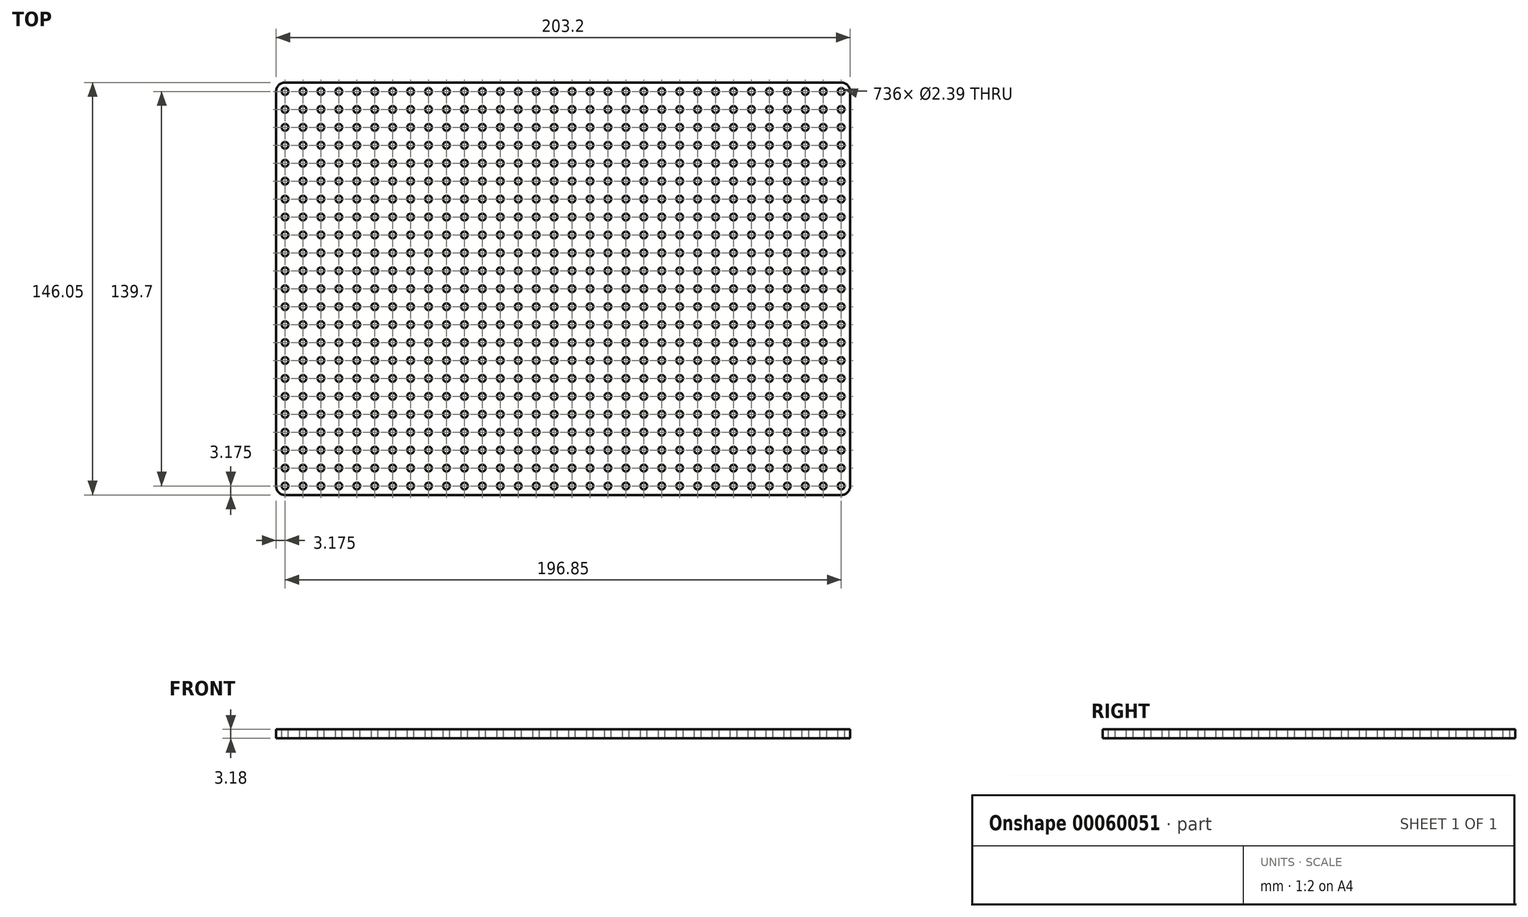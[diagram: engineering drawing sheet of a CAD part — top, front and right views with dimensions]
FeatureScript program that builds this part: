
annotation { "Feature Type Name" : "Feature", "Feature Type Description" : "" }
export const myFeature = defineFeature(function(context is Context, id is Id, definition is map)
    precondition{}
    {
        {
            var Q0;
            Q0=qCreatedBy(makeId("Top.planeOp"),FACE);
            var sketch = newSketch(context, id + "F0", { "sketchPlane" : qUnion([Q0])});
            skLineSegment(sketch, "E0.bottom", {"start": v(3.17, 0) * mm, "end": v(200.03, 0) * mm});
            skLineSegment(sketch, "E0.top", {"start": v(3.17, 146.05) * mm, "end": v(200.03, 146.05) * mm});
            skLineSegment(sketch, "E0.left", {"start": v(0, 3.17) * mm, "end": v(0, 142.87) * mm});
            skLineSegment(sketch, "E0.right", {"start": v(203.2, 3.17) * mm, "end": v(203.2, 142.87) * mm});
            skPoint(sketch, "E1.visualSharp", {"position": v(0, 146.05) * mm});
            skArc(sketch, "E1.filletArc", {"start": v(3.17, 146.05) * mm, "mid": v(0.93, 145.12) * mm, "end": v(0, 142.87) * mm});
            skPoint(sketch, "E2.visualSharp", {"position": v(203.2, 146.05) * mm});
            skArc(sketch, "E2.filletArc", {"start": v(203.2, 142.87) * mm, "mid": v(202.27, 145.12) * mm, "end": v(200.03, 146.05) * mm});
            skPoint(sketch, "E3.visualSharp", {"position": v(203.2, 0) * mm});
            skArc(sketch, "E3.filletArc", {"start": v(200.03, 0) * mm, "mid": v(202.27, 0.93) * mm, "end": v(203.2, 3.17) * mm});
            skPoint(sketch, "E4.visualSharp", {"position": v(0, 0) * mm});
            skArc(sketch, "E4.filletArc", {"start": v(0, 3.17) * mm, "mid": v(0.93, 0.93) * mm, "end": v(3.17, 0) * mm});
            skSolve(sketch);
        }
        {
            var Q0;
            Q0=makeQuery(id+"F0.imprint","IMPRINT",FACE,{"disambiguationData":[TD([[makeQuery(id+"F0.imprint","IMPRINT",EDGE,{"derivedFrom":sQuery(id+"F0.wireOp",EDGE,"E0.bottom")}),1.0]])]});
            extrude(context, id + "F1", {"entities" : qUnion([Q0]), "depth" : 3.17 * mm});
        }
        {
            var Q0;
            Q0=makeQuery(id+"F1.opExtrude","CAP_FACE",FACE,{"disambiguationData":[OSD([sQuery(id+"F0.wireOp",EDGE,"E0.bottom"),sQuery(id+"F0.wireOp",EDGE,"E0.top"),sQuery(id+"F0.wireOp",EDGE,"E0.left"),sQuery(id+"F0.wireOp",EDGE,"E0.right"),sQuery(id+"F0.wireOp",EDGE,"E1.filletArc"),sQuery(id+"F0.wireOp",EDGE,"E2.filletArc"),sQuery(id+"F0.wireOp",EDGE,"E3.filletArc"),sQuery(id+"F0.wireOp",EDGE,"E4.filletArc")])],"isStart":false});
            var sketch = newSketch(context, id + "F2", { "sketchPlane" : qUnion([Q0])});
            skCircle(sketch, "E5", {"center": v(3.17, 3.17) * mm, "radius": 1.2 * mm});
            skCircle(sketch, "E6.0.1.0", {"center": v(3.17, 9.53) * mm, "radius": 1.2 * mm});
            skCircle(sketch, "E6.0.2.0", {"center": v(3.17, 15.88) * mm, "radius": 1.2 * mm});
            skCircle(sketch, "E6.0.3.0", {"center": v(3.17, 22.23) * mm, "radius": 1.2 * mm});
            skCircle(sketch, "E6.0.4.0", {"center": v(3.17, 28.58) * mm, "radius": 1.2 * mm});
            skCircle(sketch, "E6.0.5.0", {"center": v(3.17, 34.92) * mm, "radius": 1.2 * mm});
            skCircle(sketch, "E6.0.6.0", {"center": v(3.17, 41.27) * mm, "radius": 1.2 * mm});
            skCircle(sketch, "E6.0.7.0", {"center": v(3.17, 47.62) * mm, "radius": 1.2 * mm});
            skCircle(sketch, "E6.0.8.0", {"center": v(3.17, 53.98) * mm, "radius": 1.2 * mm});
            skCircle(sketch, "E6.0.9.0", {"center": v(3.17, 60.33) * mm, "radius": 1.2 * mm});
            skCircle(sketch, "E6.0.10.0", {"center": v(3.17, 66.67) * mm, "radius": 1.2 * mm});
            skCircle(sketch, "E6.0.11.0", {"center": v(3.17, 73.03) * mm, "radius": 1.2 * mm});
            skCircle(sketch, "E6.0.12.0", {"center": v(3.17, 79.38) * mm, "radius": 1.2 * mm});
            skCircle(sketch, "E6.0.13.0", {"center": v(3.17, 85.73) * mm, "radius": 1.2 * mm});
            skCircle(sketch, "E6.0.14.0", {"center": v(3.17, 92.08) * mm, "radius": 1.2 * mm});
            skCircle(sketch, "E6.0.15.0", {"center": v(3.17, 98.43) * mm, "radius": 1.2 * mm});
            skCircle(sketch, "E6.0.16.0", {"center": v(3.17, 104.78) * mm, "radius": 1.2 * mm});
            skCircle(sketch, "E6.0.17.0", {"center": v(3.17, 111.12) * mm, "radius": 1.2 * mm});
            skCircle(sketch, "E6.0.18.0", {"center": v(3.17, 117.48) * mm, "radius": 1.2 * mm});
            skCircle(sketch, "E6.0.19.0", {"center": v(3.17, 123.83) * mm, "radius": 1.2 * mm});
            skCircle(sketch, "E6.0.20.0", {"center": v(3.17, 130.18) * mm, "radius": 1.2 * mm});
            skCircle(sketch, "E6.0.21.0", {"center": v(3.17, 136.53) * mm, "radius": 1.2 * mm});
            skCircle(sketch, "E6.0.22.0", {"center": v(3.17, 142.88) * mm, "radius": 1.2 * mm});
            skCircle(sketch, "E6.1.0.0", {"center": v(9.53, 3.17) * mm, "radius": 1.2 * mm});
            skCircle(sketch, "E6.1.1.0", {"center": v(9.53, 9.53) * mm, "radius": 1.2 * mm});
            skCircle(sketch, "E6.1.2.0", {"center": v(9.53, 15.88) * mm, "radius": 1.2 * mm});
            skCircle(sketch, "E6.1.3.0", {"center": v(9.53, 22.23) * mm, "radius": 1.2 * mm});
            skCircle(sketch, "E6.1.4.0", {"center": v(9.53, 28.58) * mm, "radius": 1.2 * mm});
            skCircle(sketch, "E6.1.5.0", {"center": v(9.53, 34.92) * mm, "radius": 1.2 * mm});
            skCircle(sketch, "E6.1.6.0", {"center": v(9.53, 41.27) * mm, "radius": 1.2 * mm});
            skCircle(sketch, "E6.1.7.0", {"center": v(9.53, 47.62) * mm, "radius": 1.2 * mm});
            skCircle(sketch, "E6.1.8.0", {"center": v(9.53, 53.98) * mm, "radius": 1.2 * mm});
            skCircle(sketch, "E6.1.9.0", {"center": v(9.53, 60.33) * mm, "radius": 1.2 * mm});
            skCircle(sketch, "E6.1.10.0", {"center": v(9.53, 66.67) * mm, "radius": 1.2 * mm});
            skCircle(sketch, "E6.1.11.0", {"center": v(9.53, 73.03) * mm, "radius": 1.2 * mm});
            skCircle(sketch, "E6.1.12.0", {"center": v(9.53, 79.38) * mm, "radius": 1.2 * mm});
            skCircle(sketch, "E6.1.13.0", {"center": v(9.53, 85.73) * mm, "radius": 1.2 * mm});
            skCircle(sketch, "E6.1.14.0", {"center": v(9.53, 92.08) * mm, "radius": 1.2 * mm});
            skCircle(sketch, "E6.1.15.0", {"center": v(9.53, 98.43) * mm, "radius": 1.2 * mm});
            skCircle(sketch, "E6.1.16.0", {"center": v(9.53, 104.78) * mm, "radius": 1.2 * mm});
            skCircle(sketch, "E6.1.17.0", {"center": v(9.53, 111.12) * mm, "radius": 1.2 * mm});
            skCircle(sketch, "E6.1.18.0", {"center": v(9.53, 117.48) * mm, "radius": 1.2 * mm});
            skCircle(sketch, "E6.1.19.0", {"center": v(9.53, 123.83) * mm, "radius": 1.2 * mm});
            skCircle(sketch, "E6.1.20.0", {"center": v(9.53, 130.18) * mm, "radius": 1.2 * mm});
            skCircle(sketch, "E6.1.21.0", {"center": v(9.53, 136.53) * mm, "radius": 1.2 * mm});
            skCircle(sketch, "E6.1.22.0", {"center": v(9.53, 142.88) * mm, "radius": 1.2 * mm});
            skCircle(sketch, "E6.2.0.0", {"center": v(15.88, 3.17) * mm, "radius": 1.2 * mm});
            skCircle(sketch, "E6.2.1.0", {"center": v(15.88, 9.53) * mm, "radius": 1.2 * mm});
            skCircle(sketch, "E6.2.2.0", {"center": v(15.88, 15.88) * mm, "radius": 1.2 * mm});
            skCircle(sketch, "E6.2.3.0", {"center": v(15.88, 22.23) * mm, "radius": 1.2 * mm});
            skCircle(sketch, "E6.2.4.0", {"center": v(15.88, 28.58) * mm, "radius": 1.2 * mm});
            skCircle(sketch, "E6.2.5.0", {"center": v(15.88, 34.92) * mm, "radius": 1.2 * mm});
            skCircle(sketch, "E6.2.6.0", {"center": v(15.88, 41.27) * mm, "radius": 1.2 * mm});
            skCircle(sketch, "E6.2.7.0", {"center": v(15.88, 47.62) * mm, "radius": 1.2 * mm});
            skCircle(sketch, "E6.2.8.0", {"center": v(15.88, 53.98) * mm, "radius": 1.2 * mm});
            skCircle(sketch, "E6.2.9.0", {"center": v(15.88, 60.33) * mm, "radius": 1.2 * mm});
            skCircle(sketch, "E6.2.10.0", {"center": v(15.88, 66.67) * mm, "radius": 1.2 * mm});
            skCircle(sketch, "E6.2.11.0", {"center": v(15.88, 73.03) * mm, "radius": 1.2 * mm});
            skCircle(sketch, "E6.2.12.0", {"center": v(15.88, 79.38) * mm, "radius": 1.2 * mm});
            skCircle(sketch, "E6.2.13.0", {"center": v(15.88, 85.73) * mm, "radius": 1.2 * mm});
            skCircle(sketch, "E6.2.14.0", {"center": v(15.88, 92.08) * mm, "radius": 1.2 * mm});
            skCircle(sketch, "E6.2.15.0", {"center": v(15.88, 98.43) * mm, "radius": 1.2 * mm});
            skCircle(sketch, "E6.2.16.0", {"center": v(15.88, 104.78) * mm, "radius": 1.2 * mm});
            skCircle(sketch, "E6.2.17.0", {"center": v(15.88, 111.12) * mm, "radius": 1.2 * mm});
            skCircle(sketch, "E6.2.18.0", {"center": v(15.88, 117.48) * mm, "radius": 1.2 * mm});
            skCircle(sketch, "E6.2.19.0", {"center": v(15.88, 123.83) * mm, "radius": 1.2 * mm});
            skCircle(sketch, "E6.2.20.0", {"center": v(15.88, 130.18) * mm, "radius": 1.2 * mm});
            skCircle(sketch, "E6.2.21.0", {"center": v(15.88, 136.53) * mm, "radius": 1.2 * mm});
            skCircle(sketch, "E6.2.22.0", {"center": v(15.88, 142.88) * mm, "radius": 1.2 * mm});
            skCircle(sketch, "E6.3.0.0", {"center": v(22.23, 3.17) * mm, "radius": 1.2 * mm});
            skCircle(sketch, "E6.3.1.0", {"center": v(22.23, 9.53) * mm, "radius": 1.2 * mm});
            skCircle(sketch, "E6.3.2.0", {"center": v(22.23, 15.88) * mm, "radius": 1.2 * mm});
            skCircle(sketch, "E6.3.3.0", {"center": v(22.23, 22.23) * mm, "radius": 1.2 * mm});
            skCircle(sketch, "E6.3.4.0", {"center": v(22.23, 28.58) * mm, "radius": 1.2 * mm});
            skCircle(sketch, "E6.3.5.0", {"center": v(22.23, 34.92) * mm, "radius": 1.2 * mm});
            skCircle(sketch, "E6.3.6.0", {"center": v(22.23, 41.27) * mm, "radius": 1.2 * mm});
            skCircle(sketch, "E6.3.7.0", {"center": v(22.23, 47.62) * mm, "radius": 1.2 * mm});
            skCircle(sketch, "E6.3.8.0", {"center": v(22.23, 53.98) * mm, "radius": 1.2 * mm});
            skCircle(sketch, "E6.3.9.0", {"center": v(22.23, 60.33) * mm, "radius": 1.2 * mm});
            skCircle(sketch, "E6.3.10.0", {"center": v(22.23, 66.67) * mm, "radius": 1.2 * mm});
            skCircle(sketch, "E6.3.11.0", {"center": v(22.23, 73.03) * mm, "radius": 1.2 * mm});
            skCircle(sketch, "E6.3.12.0", {"center": v(22.23, 79.38) * mm, "radius": 1.2 * mm});
            skCircle(sketch, "E6.3.13.0", {"center": v(22.23, 85.73) * mm, "radius": 1.2 * mm});
            skCircle(sketch, "E6.3.14.0", {"center": v(22.23, 92.08) * mm, "radius": 1.2 * mm});
            skCircle(sketch, "E6.3.15.0", {"center": v(22.23, 98.43) * mm, "radius": 1.2 * mm});
            skCircle(sketch, "E6.3.16.0", {"center": v(22.23, 104.78) * mm, "radius": 1.2 * mm});
            skCircle(sketch, "E6.3.17.0", {"center": v(22.23, 111.12) * mm, "radius": 1.2 * mm});
            skCircle(sketch, "E6.3.18.0", {"center": v(22.23, 117.48) * mm, "radius": 1.2 * mm});
            skCircle(sketch, "E6.3.19.0", {"center": v(22.23, 123.83) * mm, "radius": 1.2 * mm});
            skCircle(sketch, "E6.3.20.0", {"center": v(22.23, 130.18) * mm, "radius": 1.2 * mm});
            skCircle(sketch, "E6.3.21.0", {"center": v(22.23, 136.53) * mm, "radius": 1.2 * mm});
            skCircle(sketch, "E6.3.22.0", {"center": v(22.23, 142.88) * mm, "radius": 1.2 * mm});
            skCircle(sketch, "E6.4.0.0", {"center": v(28.58, 3.17) * mm, "radius": 1.2 * mm});
            skCircle(sketch, "E6.4.1.0", {"center": v(28.58, 9.53) * mm, "radius": 1.2 * mm});
            skCircle(sketch, "E6.4.2.0", {"center": v(28.58, 15.88) * mm, "radius": 1.2 * mm});
            skCircle(sketch, "E6.4.3.0", {"center": v(28.58, 22.23) * mm, "radius": 1.2 * mm});
            skCircle(sketch, "E6.4.4.0", {"center": v(28.58, 28.58) * mm, "radius": 1.2 * mm});
            skCircle(sketch, "E6.4.5.0", {"center": v(28.58, 34.92) * mm, "radius": 1.2 * mm});
            skCircle(sketch, "E6.4.6.0", {"center": v(28.58, 41.27) * mm, "radius": 1.2 * mm});
            skCircle(sketch, "E6.4.7.0", {"center": v(28.58, 47.62) * mm, "radius": 1.2 * mm});
            skCircle(sketch, "E6.4.8.0", {"center": v(28.58, 53.98) * mm, "radius": 1.2 * mm});
            skCircle(sketch, "E6.4.9.0", {"center": v(28.58, 60.33) * mm, "radius": 1.2 * mm});
            skCircle(sketch, "E6.4.10.0", {"center": v(28.58, 66.67) * mm, "radius": 1.2 * mm});
            skCircle(sketch, "E6.4.11.0", {"center": v(28.58, 73.03) * mm, "radius": 1.2 * mm});
            skCircle(sketch, "E6.4.12.0", {"center": v(28.58, 79.38) * mm, "radius": 1.2 * mm});
            skCircle(sketch, "E6.4.13.0", {"center": v(28.58, 85.73) * mm, "radius": 1.2 * mm});
            skCircle(sketch, "E6.4.14.0", {"center": v(28.58, 92.08) * mm, "radius": 1.2 * mm});
            skCircle(sketch, "E6.4.15.0", {"center": v(28.58, 98.43) * mm, "radius": 1.2 * mm});
            skCircle(sketch, "E6.4.16.0", {"center": v(28.58, 104.78) * mm, "radius": 1.2 * mm});
            skCircle(sketch, "E6.4.17.0", {"center": v(28.58, 111.12) * mm, "radius": 1.2 * mm});
            skCircle(sketch, "E6.4.18.0", {"center": v(28.58, 117.48) * mm, "radius": 1.2 * mm});
            skCircle(sketch, "E6.4.19.0", {"center": v(28.58, 123.83) * mm, "radius": 1.2 * mm});
            skCircle(sketch, "E6.4.20.0", {"center": v(28.58, 130.18) * mm, "radius": 1.2 * mm});
            skCircle(sketch, "E6.4.21.0", {"center": v(28.58, 136.53) * mm, "radius": 1.2 * mm});
            skCircle(sketch, "E6.4.22.0", {"center": v(28.58, 142.88) * mm, "radius": 1.2 * mm});
            skCircle(sketch, "E6.5.0.0", {"center": v(34.92, 3.17) * mm, "radius": 1.2 * mm});
            skCircle(sketch, "E6.5.1.0", {"center": v(34.92, 9.53) * mm, "radius": 1.2 * mm});
            skCircle(sketch, "E6.5.2.0", {"center": v(34.92, 15.88) * mm, "radius": 1.2 * mm});
            skCircle(sketch, "E6.5.3.0", {"center": v(34.92, 22.23) * mm, "radius": 1.2 * mm});
            skCircle(sketch, "E6.5.4.0", {"center": v(34.92, 28.58) * mm, "radius": 1.2 * mm});
            skCircle(sketch, "E6.5.5.0", {"center": v(34.92, 34.92) * mm, "radius": 1.2 * mm});
            skCircle(sketch, "E6.5.6.0", {"center": v(34.92, 41.27) * mm, "radius": 1.2 * mm});
            skCircle(sketch, "E6.5.7.0", {"center": v(34.92, 47.62) * mm, "radius": 1.2 * mm});
            skCircle(sketch, "E6.5.8.0", {"center": v(34.92, 53.98) * mm, "radius": 1.2 * mm});
            skCircle(sketch, "E6.5.9.0", {"center": v(34.92, 60.33) * mm, "radius": 1.2 * mm});
            skCircle(sketch, "E6.5.10.0", {"center": v(34.92, 66.67) * mm, "radius": 1.2 * mm});
            skCircle(sketch, "E6.5.11.0", {"center": v(34.92, 73.03) * mm, "radius": 1.2 * mm});
            skCircle(sketch, "E6.5.12.0", {"center": v(34.92, 79.38) * mm, "radius": 1.2 * mm});
            skCircle(sketch, "E6.5.13.0", {"center": v(34.92, 85.73) * mm, "radius": 1.2 * mm});
            skCircle(sketch, "E6.5.14.0", {"center": v(34.92, 92.08) * mm, "radius": 1.2 * mm});
            skCircle(sketch, "E6.5.15.0", {"center": v(34.92, 98.43) * mm, "radius": 1.2 * mm});
            skCircle(sketch, "E6.5.16.0", {"center": v(34.92, 104.78) * mm, "radius": 1.2 * mm});
            skCircle(sketch, "E6.5.17.0", {"center": v(34.92, 111.12) * mm, "radius": 1.2 * mm});
            skCircle(sketch, "E6.5.18.0", {"center": v(34.92, 117.48) * mm, "radius": 1.2 * mm});
            skCircle(sketch, "E6.5.19.0", {"center": v(34.92, 123.83) * mm, "radius": 1.2 * mm});
            skCircle(sketch, "E6.5.20.0", {"center": v(34.92, 130.18) * mm, "radius": 1.2 * mm});
            skCircle(sketch, "E6.5.21.0", {"center": v(34.92, 136.53) * mm, "radius": 1.2 * mm});
            skCircle(sketch, "E6.5.22.0", {"center": v(34.92, 142.88) * mm, "radius": 1.2 * mm});
            skCircle(sketch, "E6.6.0.0", {"center": v(41.27, 3.17) * mm, "radius": 1.2 * mm});
            skCircle(sketch, "E6.6.1.0", {"center": v(41.27, 9.53) * mm, "radius": 1.2 * mm});
            skCircle(sketch, "E6.6.2.0", {"center": v(41.27, 15.88) * mm, "radius": 1.2 * mm});
            skCircle(sketch, "E6.6.3.0", {"center": v(41.27, 22.23) * mm, "radius": 1.2 * mm});
            skCircle(sketch, "E6.6.4.0", {"center": v(41.27, 28.58) * mm, "radius": 1.2 * mm});
            skCircle(sketch, "E6.6.5.0", {"center": v(41.27, 34.92) * mm, "radius": 1.2 * mm});
            skCircle(sketch, "E6.6.6.0", {"center": v(41.27, 41.27) * mm, "radius": 1.2 * mm});
            skCircle(sketch, "E6.6.7.0", {"center": v(41.27, 47.62) * mm, "radius": 1.2 * mm});
            skCircle(sketch, "E6.6.8.0", {"center": v(41.27, 53.98) * mm, "radius": 1.2 * mm});
            skCircle(sketch, "E6.6.9.0", {"center": v(41.27, 60.33) * mm, "radius": 1.2 * mm});
            skCircle(sketch, "E6.6.10.0", {"center": v(41.27, 66.67) * mm, "radius": 1.2 * mm});
            skCircle(sketch, "E6.6.11.0", {"center": v(41.27, 73.03) * mm, "radius": 1.2 * mm});
            skCircle(sketch, "E6.6.12.0", {"center": v(41.27, 79.38) * mm, "radius": 1.2 * mm});
            skCircle(sketch, "E6.6.13.0", {"center": v(41.27, 85.73) * mm, "radius": 1.2 * mm});
            skCircle(sketch, "E6.6.14.0", {"center": v(41.27, 92.08) * mm, "radius": 1.2 * mm});
            skCircle(sketch, "E6.6.15.0", {"center": v(41.27, 98.43) * mm, "radius": 1.2 * mm});
            skCircle(sketch, "E6.6.16.0", {"center": v(41.27, 104.78) * mm, "radius": 1.2 * mm});
            skCircle(sketch, "E6.6.17.0", {"center": v(41.27, 111.12) * mm, "radius": 1.2 * mm});
            skCircle(sketch, "E6.6.18.0", {"center": v(41.27, 117.48) * mm, "radius": 1.2 * mm});
            skCircle(sketch, "E6.6.19.0", {"center": v(41.27, 123.83) * mm, "radius": 1.2 * mm});
            skCircle(sketch, "E6.6.20.0", {"center": v(41.27, 130.18) * mm, "radius": 1.2 * mm});
            skCircle(sketch, "E6.6.21.0", {"center": v(41.27, 136.53) * mm, "radius": 1.2 * mm});
            skCircle(sketch, "E6.6.22.0", {"center": v(41.27, 142.88) * mm, "radius": 1.2 * mm});
            skCircle(sketch, "E6.7.0.0", {"center": v(47.62, 3.17) * mm, "radius": 1.2 * mm});
            skCircle(sketch, "E6.7.1.0", {"center": v(47.62, 9.53) * mm, "radius": 1.2 * mm});
            skCircle(sketch, "E6.7.2.0", {"center": v(47.62, 15.88) * mm, "radius": 1.2 * mm});
            skCircle(sketch, "E6.7.3.0", {"center": v(47.62, 22.23) * mm, "radius": 1.2 * mm});
            skCircle(sketch, "E6.7.4.0", {"center": v(47.62, 28.58) * mm, "radius": 1.2 * mm});
            skCircle(sketch, "E6.7.5.0", {"center": v(47.62, 34.92) * mm, "radius": 1.2 * mm});
            skCircle(sketch, "E6.7.6.0", {"center": v(47.62, 41.27) * mm, "radius": 1.2 * mm});
            skCircle(sketch, "E6.7.7.0", {"center": v(47.62, 47.62) * mm, "radius": 1.2 * mm});
            skCircle(sketch, "E6.7.8.0", {"center": v(47.62, 53.98) * mm, "radius": 1.2 * mm});
            skCircle(sketch, "E6.7.9.0", {"center": v(47.62, 60.33) * mm, "radius": 1.2 * mm});
            skCircle(sketch, "E6.7.10.0", {"center": v(47.62, 66.67) * mm, "radius": 1.2 * mm});
            skCircle(sketch, "E6.7.11.0", {"center": v(47.62, 73.03) * mm, "radius": 1.2 * mm});
            skCircle(sketch, "E6.7.12.0", {"center": v(47.62, 79.38) * mm, "radius": 1.2 * mm});
            skCircle(sketch, "E6.7.13.0", {"center": v(47.62, 85.73) * mm, "radius": 1.2 * mm});
            skCircle(sketch, "E6.7.14.0", {"center": v(47.62, 92.08) * mm, "radius": 1.2 * mm});
            skCircle(sketch, "E6.7.15.0", {"center": v(47.62, 98.43) * mm, "radius": 1.2 * mm});
            skCircle(sketch, "E6.7.16.0", {"center": v(47.62, 104.78) * mm, "radius": 1.2 * mm});
            skCircle(sketch, "E6.7.17.0", {"center": v(47.62, 111.12) * mm, "radius": 1.2 * mm});
            skCircle(sketch, "E6.7.18.0", {"center": v(47.62, 117.48) * mm, "radius": 1.2 * mm});
            skCircle(sketch, "E6.7.19.0", {"center": v(47.62, 123.83) * mm, "radius": 1.2 * mm});
            skCircle(sketch, "E6.7.20.0", {"center": v(47.62, 130.18) * mm, "radius": 1.2 * mm});
            skCircle(sketch, "E6.7.21.0", {"center": v(47.62, 136.53) * mm, "radius": 1.2 * mm});
            skCircle(sketch, "E6.7.22.0", {"center": v(47.62, 142.88) * mm, "radius": 1.2 * mm});
            skCircle(sketch, "E6.8.0.0", {"center": v(53.98, 3.17) * mm, "radius": 1.2 * mm});
            skCircle(sketch, "E6.8.1.0", {"center": v(53.98, 9.53) * mm, "radius": 1.2 * mm});
            skCircle(sketch, "E6.8.2.0", {"center": v(53.98, 15.88) * mm, "radius": 1.2 * mm});
            skCircle(sketch, "E6.8.3.0", {"center": v(53.98, 22.23) * mm, "radius": 1.2 * mm});
            skCircle(sketch, "E6.8.4.0", {"center": v(53.98, 28.58) * mm, "radius": 1.2 * mm});
            skCircle(sketch, "E6.8.5.0", {"center": v(53.98, 34.92) * mm, "radius": 1.2 * mm});
            skCircle(sketch, "E6.8.6.0", {"center": v(53.98, 41.27) * mm, "radius": 1.2 * mm});
            skCircle(sketch, "E6.8.7.0", {"center": v(53.98, 47.62) * mm, "radius": 1.2 * mm});
            skCircle(sketch, "E6.8.8.0", {"center": v(53.98, 53.98) * mm, "radius": 1.2 * mm});
            skCircle(sketch, "E6.8.9.0", {"center": v(53.98, 60.33) * mm, "radius": 1.2 * mm});
            skCircle(sketch, "E6.8.10.0", {"center": v(53.98, 66.67) * mm, "radius": 1.2 * mm});
            skCircle(sketch, "E6.8.11.0", {"center": v(53.98, 73.03) * mm, "radius": 1.2 * mm});
            skCircle(sketch, "E6.8.12.0", {"center": v(53.98, 79.38) * mm, "radius": 1.2 * mm});
            skCircle(sketch, "E6.8.13.0", {"center": v(53.98, 85.73) * mm, "radius": 1.2 * mm});
            skCircle(sketch, "E6.8.14.0", {"center": v(53.98, 92.08) * mm, "radius": 1.2 * mm});
            skCircle(sketch, "E6.8.15.0", {"center": v(53.98, 98.43) * mm, "radius": 1.2 * mm});
            skCircle(sketch, "E6.8.16.0", {"center": v(53.98, 104.78) * mm, "radius": 1.2 * mm});
            skCircle(sketch, "E6.8.17.0", {"center": v(53.98, 111.12) * mm, "radius": 1.2 * mm});
            skCircle(sketch, "E6.8.18.0", {"center": v(53.98, 117.48) * mm, "radius": 1.2 * mm});
            skCircle(sketch, "E6.8.19.0", {"center": v(53.98, 123.83) * mm, "radius": 1.2 * mm});
            skCircle(sketch, "E6.8.20.0", {"center": v(53.98, 130.18) * mm, "radius": 1.2 * mm});
            skCircle(sketch, "E6.8.21.0", {"center": v(53.98, 136.53) * mm, "radius": 1.2 * mm});
            skCircle(sketch, "E6.8.22.0", {"center": v(53.98, 142.88) * mm, "radius": 1.2 * mm});
            skCircle(sketch, "E6.9.0.0", {"center": v(60.33, 3.17) * mm, "radius": 1.2 * mm});
            skCircle(sketch, "E6.9.1.0", {"center": v(60.33, 9.53) * mm, "radius": 1.2 * mm});
            skCircle(sketch, "E6.9.2.0", {"center": v(60.33, 15.88) * mm, "radius": 1.2 * mm});
            skCircle(sketch, "E6.9.3.0", {"center": v(60.33, 22.23) * mm, "radius": 1.2 * mm});
            skCircle(sketch, "E6.9.4.0", {"center": v(60.33, 28.58) * mm, "radius": 1.2 * mm});
            skCircle(sketch, "E6.9.5.0", {"center": v(60.33, 34.92) * mm, "radius": 1.2 * mm});
            skCircle(sketch, "E6.9.6.0", {"center": v(60.33, 41.27) * mm, "radius": 1.2 * mm});
            skCircle(sketch, "E6.9.7.0", {"center": v(60.33, 47.62) * mm, "radius": 1.2 * mm});
            skCircle(sketch, "E6.9.8.0", {"center": v(60.33, 53.98) * mm, "radius": 1.2 * mm});
            skCircle(sketch, "E6.9.9.0", {"center": v(60.33, 60.33) * mm, "radius": 1.2 * mm});
            skCircle(sketch, "E6.9.10.0", {"center": v(60.33, 66.67) * mm, "radius": 1.2 * mm});
            skCircle(sketch, "E6.9.11.0", {"center": v(60.33, 73.03) * mm, "radius": 1.2 * mm});
            skCircle(sketch, "E6.9.12.0", {"center": v(60.33, 79.38) * mm, "radius": 1.2 * mm});
            skCircle(sketch, "E6.9.13.0", {"center": v(60.33, 85.73) * mm, "radius": 1.2 * mm});
            skCircle(sketch, "E6.9.14.0", {"center": v(60.33, 92.08) * mm, "radius": 1.2 * mm});
            skCircle(sketch, "E6.9.15.0", {"center": v(60.33, 98.43) * mm, "radius": 1.2 * mm});
            skCircle(sketch, "E6.9.16.0", {"center": v(60.33, 104.78) * mm, "radius": 1.2 * mm});
            skCircle(sketch, "E6.9.17.0", {"center": v(60.33, 111.12) * mm, "radius": 1.2 * mm});
            skCircle(sketch, "E6.9.18.0", {"center": v(60.33, 117.48) * mm, "radius": 1.2 * mm});
            skCircle(sketch, "E6.9.19.0", {"center": v(60.33, 123.83) * mm, "radius": 1.2 * mm});
            skCircle(sketch, "E6.9.20.0", {"center": v(60.33, 130.18) * mm, "radius": 1.2 * mm});
            skCircle(sketch, "E6.9.21.0", {"center": v(60.33, 136.53) * mm, "radius": 1.2 * mm});
            skCircle(sketch, "E6.9.22.0", {"center": v(60.33, 142.88) * mm, "radius": 1.2 * mm});
            skCircle(sketch, "E6.10.0.0", {"center": v(66.67, 3.17) * mm, "radius": 1.2 * mm});
            skCircle(sketch, "E6.10.1.0", {"center": v(66.67, 9.53) * mm, "radius": 1.2 * mm});
            skCircle(sketch, "E6.10.2.0", {"center": v(66.67, 15.88) * mm, "radius": 1.2 * mm});
            skCircle(sketch, "E6.10.3.0", {"center": v(66.67, 22.23) * mm, "radius": 1.2 * mm});
            skCircle(sketch, "E6.10.4.0", {"center": v(66.67, 28.58) * mm, "radius": 1.2 * mm});
            skCircle(sketch, "E6.10.5.0", {"center": v(66.67, 34.92) * mm, "radius": 1.2 * mm});
            skCircle(sketch, "E6.10.6.0", {"center": v(66.67, 41.27) * mm, "radius": 1.2 * mm});
            skCircle(sketch, "E6.10.7.0", {"center": v(66.67, 47.62) * mm, "radius": 1.2 * mm});
            skCircle(sketch, "E6.10.8.0", {"center": v(66.67, 53.98) * mm, "radius": 1.2 * mm});
            skCircle(sketch, "E6.10.9.0", {"center": v(66.67, 60.33) * mm, "radius": 1.2 * mm});
            skCircle(sketch, "E6.10.10.0", {"center": v(66.67, 66.67) * mm, "radius": 1.2 * mm});
            skCircle(sketch, "E6.10.11.0", {"center": v(66.67, 73.03) * mm, "radius": 1.2 * mm});
            skCircle(sketch, "E6.10.12.0", {"center": v(66.67, 79.38) * mm, "radius": 1.2 * mm});
            skCircle(sketch, "E6.10.13.0", {"center": v(66.67, 85.73) * mm, "radius": 1.2 * mm});
            skCircle(sketch, "E6.10.14.0", {"center": v(66.67, 92.08) * mm, "radius": 1.2 * mm});
            skCircle(sketch, "E6.10.15.0", {"center": v(66.67, 98.43) * mm, "radius": 1.2 * mm});
            skCircle(sketch, "E6.10.16.0", {"center": v(66.67, 104.78) * mm, "radius": 1.2 * mm});
            skCircle(sketch, "E6.10.17.0", {"center": v(66.67, 111.12) * mm, "radius": 1.2 * mm});
            skCircle(sketch, "E6.10.18.0", {"center": v(66.67, 117.48) * mm, "radius": 1.2 * mm});
            skCircle(sketch, "E6.10.19.0", {"center": v(66.67, 123.83) * mm, "radius": 1.2 * mm});
            skCircle(sketch, "E6.10.20.0", {"center": v(66.67, 130.18) * mm, "radius": 1.2 * mm});
            skCircle(sketch, "E6.10.21.0", {"center": v(66.67, 136.53) * mm, "radius": 1.2 * mm});
            skCircle(sketch, "E6.10.22.0", {"center": v(66.67, 142.88) * mm, "radius": 1.2 * mm});
            skCircle(sketch, "E6.11.0.0", {"center": v(73.03, 3.17) * mm, "radius": 1.2 * mm});
            skCircle(sketch, "E6.11.1.0", {"center": v(73.03, 9.53) * mm, "radius": 1.2 * mm});
            skCircle(sketch, "E6.11.2.0", {"center": v(73.03, 15.88) * mm, "radius": 1.2 * mm});
            skCircle(sketch, "E6.11.3.0", {"center": v(73.03, 22.23) * mm, "radius": 1.2 * mm});
            skCircle(sketch, "E6.11.4.0", {"center": v(73.03, 28.58) * mm, "radius": 1.2 * mm});
            skCircle(sketch, "E6.11.5.0", {"center": v(73.03, 34.92) * mm, "radius": 1.2 * mm});
            skCircle(sketch, "E6.11.6.0", {"center": v(73.03, 41.27) * mm, "radius": 1.2 * mm});
            skCircle(sketch, "E6.11.7.0", {"center": v(73.03, 47.62) * mm, "radius": 1.2 * mm});
            skCircle(sketch, "E6.11.8.0", {"center": v(73.03, 53.98) * mm, "radius": 1.2 * mm});
            skCircle(sketch, "E6.11.9.0", {"center": v(73.03, 60.33) * mm, "radius": 1.2 * mm});
            skCircle(sketch, "E6.11.10.0", {"center": v(73.03, 66.67) * mm, "radius": 1.2 * mm});
            skCircle(sketch, "E6.11.11.0", {"center": v(73.03, 73.03) * mm, "radius": 1.2 * mm});
            skCircle(sketch, "E6.11.12.0", {"center": v(73.03, 79.38) * mm, "radius": 1.2 * mm});
            skCircle(sketch, "E6.11.13.0", {"center": v(73.03, 85.73) * mm, "radius": 1.2 * mm});
            skCircle(sketch, "E6.11.14.0", {"center": v(73.03, 92.08) * mm, "radius": 1.2 * mm});
            skCircle(sketch, "E6.11.15.0", {"center": v(73.03, 98.43) * mm, "radius": 1.2 * mm});
            skCircle(sketch, "E6.11.16.0", {"center": v(73.03, 104.78) * mm, "radius": 1.2 * mm});
            skCircle(sketch, "E6.11.17.0", {"center": v(73.03, 111.12) * mm, "radius": 1.2 * mm});
            skCircle(sketch, "E6.11.18.0", {"center": v(73.03, 117.48) * mm, "radius": 1.2 * mm});
            skCircle(sketch, "E6.11.19.0", {"center": v(73.03, 123.83) * mm, "radius": 1.2 * mm});
            skCircle(sketch, "E6.11.20.0", {"center": v(73.03, 130.18) * mm, "radius": 1.2 * mm});
            skCircle(sketch, "E6.11.21.0", {"center": v(73.03, 136.53) * mm, "radius": 1.2 * mm});
            skCircle(sketch, "E6.11.22.0", {"center": v(73.03, 142.88) * mm, "radius": 1.2 * mm});
            skCircle(sketch, "E6.12.0.0", {"center": v(79.38, 3.17) * mm, "radius": 1.2 * mm});
            skCircle(sketch, "E6.12.1.0", {"center": v(79.38, 9.53) * mm, "radius": 1.2 * mm});
            skCircle(sketch, "E6.12.2.0", {"center": v(79.38, 15.88) * mm, "radius": 1.2 * mm});
            skCircle(sketch, "E6.12.3.0", {"center": v(79.38, 22.23) * mm, "radius": 1.2 * mm});
            skCircle(sketch, "E6.12.4.0", {"center": v(79.38, 28.58) * mm, "radius": 1.2 * mm});
            skCircle(sketch, "E6.12.5.0", {"center": v(79.38, 34.92) * mm, "radius": 1.2 * mm});
            skCircle(sketch, "E6.12.6.0", {"center": v(79.38, 41.27) * mm, "radius": 1.2 * mm});
            skCircle(sketch, "E6.12.7.0", {"center": v(79.38, 47.62) * mm, "radius": 1.2 * mm});
            skCircle(sketch, "E6.12.8.0", {"center": v(79.38, 53.98) * mm, "radius": 1.2 * mm});
            skCircle(sketch, "E6.12.9.0", {"center": v(79.38, 60.33) * mm, "radius": 1.2 * mm});
            skCircle(sketch, "E6.12.10.0", {"center": v(79.38, 66.67) * mm, "radius": 1.2 * mm});
            skCircle(sketch, "E6.12.11.0", {"center": v(79.38, 73.03) * mm, "radius": 1.2 * mm});
            skCircle(sketch, "E6.12.12.0", {"center": v(79.38, 79.38) * mm, "radius": 1.2 * mm});
            skCircle(sketch, "E6.12.13.0", {"center": v(79.38, 85.73) * mm, "radius": 1.2 * mm});
            skCircle(sketch, "E6.12.14.0", {"center": v(79.38, 92.08) * mm, "radius": 1.2 * mm});
            skCircle(sketch, "E6.12.15.0", {"center": v(79.38, 98.43) * mm, "radius": 1.2 * mm});
            skCircle(sketch, "E6.12.16.0", {"center": v(79.38, 104.78) * mm, "radius": 1.2 * mm});
            skCircle(sketch, "E6.12.17.0", {"center": v(79.38, 111.12) * mm, "radius": 1.2 * mm});
            skCircle(sketch, "E6.12.18.0", {"center": v(79.38, 117.48) * mm, "radius": 1.2 * mm});
            skCircle(sketch, "E6.12.19.0", {"center": v(79.38, 123.83) * mm, "radius": 1.2 * mm});
            skCircle(sketch, "E6.12.20.0", {"center": v(79.38, 130.18) * mm, "radius": 1.2 * mm});
            skCircle(sketch, "E6.12.21.0", {"center": v(79.38, 136.53) * mm, "radius": 1.2 * mm});
            skCircle(sketch, "E6.12.22.0", {"center": v(79.38, 142.88) * mm, "radius": 1.2 * mm});
            skCircle(sketch, "E6.13.0.0", {"center": v(85.73, 3.17) * mm, "radius": 1.2 * mm});
            skCircle(sketch, "E6.13.1.0", {"center": v(85.73, 9.53) * mm, "radius": 1.2 * mm});
            skCircle(sketch, "E6.13.2.0", {"center": v(85.73, 15.88) * mm, "radius": 1.2 * mm});
            skCircle(sketch, "E6.13.3.0", {"center": v(85.73, 22.23) * mm, "radius": 1.2 * mm});
            skCircle(sketch, "E6.13.4.0", {"center": v(85.73, 28.58) * mm, "radius": 1.2 * mm});
            skCircle(sketch, "E6.13.5.0", {"center": v(85.73, 34.92) * mm, "radius": 1.2 * mm});
            skCircle(sketch, "E6.13.6.0", {"center": v(85.73, 41.27) * mm, "radius": 1.2 * mm});
            skCircle(sketch, "E6.13.7.0", {"center": v(85.73, 47.62) * mm, "radius": 1.2 * mm});
            skCircle(sketch, "E6.13.8.0", {"center": v(85.73, 53.98) * mm, "radius": 1.2 * mm});
            skCircle(sketch, "E6.13.9.0", {"center": v(85.73, 60.33) * mm, "radius": 1.2 * mm});
            skCircle(sketch, "E6.13.10.0", {"center": v(85.73, 66.67) * mm, "radius": 1.2 * mm});
            skCircle(sketch, "E6.13.11.0", {"center": v(85.73, 73.03) * mm, "radius": 1.2 * mm});
            skCircle(sketch, "E6.13.12.0", {"center": v(85.73, 79.38) * mm, "radius": 1.2 * mm});
            skCircle(sketch, "E6.13.13.0", {"center": v(85.73, 85.73) * mm, "radius": 1.2 * mm});
            skCircle(sketch, "E6.13.14.0", {"center": v(85.73, 92.08) * mm, "radius": 1.2 * mm});
            skCircle(sketch, "E6.13.15.0", {"center": v(85.73, 98.43) * mm, "radius": 1.2 * mm});
            skCircle(sketch, "E6.13.16.0", {"center": v(85.73, 104.78) * mm, "radius": 1.2 * mm});
            skCircle(sketch, "E6.13.17.0", {"center": v(85.73, 111.12) * mm, "radius": 1.2 * mm});
            skCircle(sketch, "E6.13.18.0", {"center": v(85.73, 117.48) * mm, "radius": 1.2 * mm});
            skCircle(sketch, "E6.13.19.0", {"center": v(85.73, 123.83) * mm, "radius": 1.2 * mm});
            skCircle(sketch, "E6.13.20.0", {"center": v(85.73, 130.18) * mm, "radius": 1.2 * mm});
            skCircle(sketch, "E6.13.21.0", {"center": v(85.73, 136.53) * mm, "radius": 1.2 * mm});
            skCircle(sketch, "E6.13.22.0", {"center": v(85.73, 142.88) * mm, "radius": 1.2 * mm});
            skCircle(sketch, "E6.14.0.0", {"center": v(92.08, 3.17) * mm, "radius": 1.2 * mm});
            skCircle(sketch, "E6.14.1.0", {"center": v(92.08, 9.53) * mm, "radius": 1.2 * mm});
            skCircle(sketch, "E6.14.2.0", {"center": v(92.08, 15.88) * mm, "radius": 1.2 * mm});
            skCircle(sketch, "E6.14.3.0", {"center": v(92.08, 22.23) * mm, "radius": 1.2 * mm});
            skCircle(sketch, "E6.14.4.0", {"center": v(92.08, 28.58) * mm, "radius": 1.2 * mm});
            skCircle(sketch, "E6.14.5.0", {"center": v(92.08, 34.92) * mm, "radius": 1.2 * mm});
            skCircle(sketch, "E6.14.6.0", {"center": v(92.08, 41.27) * mm, "radius": 1.2 * mm});
            skCircle(sketch, "E6.14.7.0", {"center": v(92.08, 47.62) * mm, "radius": 1.2 * mm});
            skCircle(sketch, "E6.14.8.0", {"center": v(92.08, 53.98) * mm, "radius": 1.2 * mm});
            skCircle(sketch, "E6.14.9.0", {"center": v(92.08, 60.33) * mm, "radius": 1.2 * mm});
            skCircle(sketch, "E6.14.10.0", {"center": v(92.08, 66.67) * mm, "radius": 1.2 * mm});
            skCircle(sketch, "E6.14.11.0", {"center": v(92.08, 73.03) * mm, "radius": 1.2 * mm});
            skCircle(sketch, "E6.14.12.0", {"center": v(92.08, 79.38) * mm, "radius": 1.2 * mm});
            skCircle(sketch, "E6.14.13.0", {"center": v(92.08, 85.73) * mm, "radius": 1.2 * mm});
            skCircle(sketch, "E6.14.14.0", {"center": v(92.08, 92.08) * mm, "radius": 1.2 * mm});
            skCircle(sketch, "E6.14.15.0", {"center": v(92.08, 98.43) * mm, "radius": 1.2 * mm});
            skCircle(sketch, "E6.14.16.0", {"center": v(92.08, 104.78) * mm, "radius": 1.2 * mm});
            skCircle(sketch, "E6.14.17.0", {"center": v(92.08, 111.12) * mm, "radius": 1.2 * mm});
            skCircle(sketch, "E6.14.18.0", {"center": v(92.08, 117.48) * mm, "radius": 1.2 * mm});
            skCircle(sketch, "E6.14.19.0", {"center": v(92.08, 123.83) * mm, "radius": 1.2 * mm});
            skCircle(sketch, "E6.14.20.0", {"center": v(92.08, 130.18) * mm, "radius": 1.2 * mm});
            skCircle(sketch, "E6.14.21.0", {"center": v(92.08, 136.53) * mm, "radius": 1.2 * mm});
            skCircle(sketch, "E6.14.22.0", {"center": v(92.08, 142.88) * mm, "radius": 1.2 * mm});
            skCircle(sketch, "E6.15.0.0", {"center": v(98.43, 3.17) * mm, "radius": 1.2 * mm});
            skCircle(sketch, "E6.15.1.0", {"center": v(98.43, 9.53) * mm, "radius": 1.2 * mm});
            skCircle(sketch, "E6.15.2.0", {"center": v(98.43, 15.88) * mm, "radius": 1.2 * mm});
            skCircle(sketch, "E6.15.3.0", {"center": v(98.43, 22.23) * mm, "radius": 1.2 * mm});
            skCircle(sketch, "E6.15.4.0", {"center": v(98.43, 28.58) * mm, "radius": 1.2 * mm});
            skCircle(sketch, "E6.15.5.0", {"center": v(98.43, 34.92) * mm, "radius": 1.2 * mm});
            skCircle(sketch, "E6.15.6.0", {"center": v(98.43, 41.27) * mm, "radius": 1.2 * mm});
            skCircle(sketch, "E6.15.7.0", {"center": v(98.43, 47.62) * mm, "radius": 1.2 * mm});
            skCircle(sketch, "E6.15.8.0", {"center": v(98.43, 53.98) * mm, "radius": 1.2 * mm});
            skCircle(sketch, "E6.15.9.0", {"center": v(98.43, 60.33) * mm, "radius": 1.2 * mm});
            skCircle(sketch, "E6.15.10.0", {"center": v(98.43, 66.67) * mm, "radius": 1.2 * mm});
            skCircle(sketch, "E6.15.11.0", {"center": v(98.43, 73.03) * mm, "radius": 1.2 * mm});
            skCircle(sketch, "E6.15.12.0", {"center": v(98.43, 79.38) * mm, "radius": 1.2 * mm});
            skCircle(sketch, "E6.15.13.0", {"center": v(98.43, 85.73) * mm, "radius": 1.2 * mm});
            skCircle(sketch, "E6.15.14.0", {"center": v(98.43, 92.08) * mm, "radius": 1.2 * mm});
            skCircle(sketch, "E6.15.15.0", {"center": v(98.43, 98.43) * mm, "radius": 1.2 * mm});
            skCircle(sketch, "E6.15.16.0", {"center": v(98.43, 104.78) * mm, "radius": 1.2 * mm});
            skCircle(sketch, "E6.15.17.0", {"center": v(98.43, 111.12) * mm, "radius": 1.2 * mm});
            skCircle(sketch, "E6.15.18.0", {"center": v(98.43, 117.48) * mm, "radius": 1.2 * mm});
            skCircle(sketch, "E6.15.19.0", {"center": v(98.43, 123.83) * mm, "radius": 1.2 * mm});
            skCircle(sketch, "E6.15.20.0", {"center": v(98.43, 130.18) * mm, "radius": 1.2 * mm});
            skCircle(sketch, "E6.15.21.0", {"center": v(98.43, 136.53) * mm, "radius": 1.2 * mm});
            skCircle(sketch, "E6.15.22.0", {"center": v(98.43, 142.88) * mm, "radius": 1.2 * mm});
            skCircle(sketch, "E6.16.0.0", {"center": v(104.78, 3.17) * mm, "radius": 1.2 * mm});
            skCircle(sketch, "E6.16.1.0", {"center": v(104.78, 9.53) * mm, "radius": 1.2 * mm});
            skCircle(sketch, "E6.16.2.0", {"center": v(104.78, 15.88) * mm, "radius": 1.2 * mm});
            skCircle(sketch, "E6.16.3.0", {"center": v(104.78, 22.23) * mm, "radius": 1.2 * mm});
            skCircle(sketch, "E6.16.4.0", {"center": v(104.78, 28.58) * mm, "radius": 1.2 * mm});
            skCircle(sketch, "E6.16.5.0", {"center": v(104.78, 34.92) * mm, "radius": 1.2 * mm});
            skCircle(sketch, "E6.16.6.0", {"center": v(104.78, 41.27) * mm, "radius": 1.2 * mm});
            skCircle(sketch, "E6.16.7.0", {"center": v(104.78, 47.62) * mm, "radius": 1.2 * mm});
            skCircle(sketch, "E6.16.8.0", {"center": v(104.78, 53.98) * mm, "radius": 1.2 * mm});
            skCircle(sketch, "E6.16.9.0", {"center": v(104.78, 60.33) * mm, "radius": 1.2 * mm});
            skCircle(sketch, "E6.16.10.0", {"center": v(104.78, 66.67) * mm, "radius": 1.2 * mm});
            skCircle(sketch, "E6.16.11.0", {"center": v(104.78, 73.03) * mm, "radius": 1.2 * mm});
            skCircle(sketch, "E6.16.12.0", {"center": v(104.78, 79.38) * mm, "radius": 1.2 * mm});
            skCircle(sketch, "E6.16.13.0", {"center": v(104.78, 85.73) * mm, "radius": 1.2 * mm});
            skCircle(sketch, "E6.16.14.0", {"center": v(104.78, 92.08) * mm, "radius": 1.2 * mm});
            skCircle(sketch, "E6.16.15.0", {"center": v(104.78, 98.43) * mm, "radius": 1.2 * mm});
            skCircle(sketch, "E6.16.16.0", {"center": v(104.78, 104.78) * mm, "radius": 1.2 * mm});
            skCircle(sketch, "E6.16.17.0", {"center": v(104.78, 111.12) * mm, "radius": 1.2 * mm});
            skCircle(sketch, "E6.16.18.0", {"center": v(104.78, 117.48) * mm, "radius": 1.2 * mm});
            skCircle(sketch, "E6.16.19.0", {"center": v(104.78, 123.83) * mm, "radius": 1.2 * mm});
            skCircle(sketch, "E6.16.20.0", {"center": v(104.78, 130.18) * mm, "radius": 1.2 * mm});
            skCircle(sketch, "E6.16.21.0", {"center": v(104.78, 136.53) * mm, "radius": 1.2 * mm});
            skCircle(sketch, "E6.16.22.0", {"center": v(104.78, 142.88) * mm, "radius": 1.2 * mm});
            skCircle(sketch, "E6.17.0.0", {"center": v(111.12, 3.17) * mm, "radius": 1.2 * mm});
            skCircle(sketch, "E6.17.1.0", {"center": v(111.12, 9.53) * mm, "radius": 1.2 * mm});
            skCircle(sketch, "E6.17.2.0", {"center": v(111.12, 15.88) * mm, "radius": 1.2 * mm});
            skCircle(sketch, "E6.17.3.0", {"center": v(111.12, 22.23) * mm, "radius": 1.2 * mm});
            skCircle(sketch, "E6.17.4.0", {"center": v(111.12, 28.58) * mm, "radius": 1.2 * mm});
            skCircle(sketch, "E6.17.5.0", {"center": v(111.12, 34.92) * mm, "radius": 1.2 * mm});
            skCircle(sketch, "E6.17.6.0", {"center": v(111.12, 41.27) * mm, "radius": 1.2 * mm});
            skCircle(sketch, "E6.17.7.0", {"center": v(111.12, 47.62) * mm, "radius": 1.2 * mm});
            skCircle(sketch, "E6.17.8.0", {"center": v(111.12, 53.98) * mm, "radius": 1.2 * mm});
            skCircle(sketch, "E6.17.9.0", {"center": v(111.12, 60.33) * mm, "radius": 1.2 * mm});
            skCircle(sketch, "E6.17.10.0", {"center": v(111.12, 66.67) * mm, "radius": 1.2 * mm});
            skCircle(sketch, "E6.17.11.0", {"center": v(111.12, 73.03) * mm, "radius": 1.2 * mm});
            skCircle(sketch, "E6.17.12.0", {"center": v(111.12, 79.38) * mm, "radius": 1.2 * mm});
            skCircle(sketch, "E6.17.13.0", {"center": v(111.12, 85.73) * mm, "radius": 1.2 * mm});
            skCircle(sketch, "E6.17.14.0", {"center": v(111.12, 92.08) * mm, "radius": 1.2 * mm});
            skCircle(sketch, "E6.17.15.0", {"center": v(111.12, 98.43) * mm, "radius": 1.2 * mm});
            skCircle(sketch, "E6.17.16.0", {"center": v(111.12, 104.78) * mm, "radius": 1.2 * mm});
            skCircle(sketch, "E6.17.17.0", {"center": v(111.12, 111.12) * mm, "radius": 1.2 * mm});
            skCircle(sketch, "E6.17.18.0", {"center": v(111.12, 117.48) * mm, "radius": 1.2 * mm});
            skCircle(sketch, "E6.17.19.0", {"center": v(111.12, 123.83) * mm, "radius": 1.2 * mm});
            skCircle(sketch, "E6.17.20.0", {"center": v(111.12, 130.18) * mm, "radius": 1.2 * mm});
            skCircle(sketch, "E6.17.21.0", {"center": v(111.12, 136.53) * mm, "radius": 1.2 * mm});
            skCircle(sketch, "E6.17.22.0", {"center": v(111.12, 142.88) * mm, "radius": 1.2 * mm});
            skCircle(sketch, "E6.18.0.0", {"center": v(117.48, 3.17) * mm, "radius": 1.2 * mm});
            skCircle(sketch, "E6.18.1.0", {"center": v(117.48, 9.53) * mm, "radius": 1.2 * mm});
            skCircle(sketch, "E6.18.2.0", {"center": v(117.48, 15.88) * mm, "radius": 1.2 * mm});
            skCircle(sketch, "E6.18.3.0", {"center": v(117.48, 22.23) * mm, "radius": 1.2 * mm});
            skCircle(sketch, "E6.18.4.0", {"center": v(117.48, 28.58) * mm, "radius": 1.2 * mm});
            skCircle(sketch, "E6.18.5.0", {"center": v(117.48, 34.92) * mm, "radius": 1.2 * mm});
            skCircle(sketch, "E6.18.6.0", {"center": v(117.48, 41.27) * mm, "radius": 1.2 * mm});
            skCircle(sketch, "E6.18.7.0", {"center": v(117.48, 47.62) * mm, "radius": 1.2 * mm});
            skCircle(sketch, "E6.18.8.0", {"center": v(117.48, 53.98) * mm, "radius": 1.2 * mm});
            skCircle(sketch, "E6.18.9.0", {"center": v(117.48, 60.33) * mm, "radius": 1.2 * mm});
            skCircle(sketch, "E6.18.10.0", {"center": v(117.48, 66.67) * mm, "radius": 1.2 * mm});
            skCircle(sketch, "E6.18.11.0", {"center": v(117.48, 73.03) * mm, "radius": 1.2 * mm});
            skCircle(sketch, "E6.18.12.0", {"center": v(117.48, 79.38) * mm, "radius": 1.2 * mm});
            skCircle(sketch, "E6.18.13.0", {"center": v(117.48, 85.73) * mm, "radius": 1.2 * mm});
            skCircle(sketch, "E6.18.14.0", {"center": v(117.48, 92.08) * mm, "radius": 1.2 * mm});
            skCircle(sketch, "E6.18.15.0", {"center": v(117.48, 98.43) * mm, "radius": 1.2 * mm});
            skCircle(sketch, "E6.18.16.0", {"center": v(117.48, 104.78) * mm, "radius": 1.2 * mm});
            skCircle(sketch, "E6.18.17.0", {"center": v(117.48, 111.12) * mm, "radius": 1.2 * mm});
            skCircle(sketch, "E6.18.18.0", {"center": v(117.48, 117.48) * mm, "radius": 1.2 * mm});
            skCircle(sketch, "E6.18.19.0", {"center": v(117.48, 123.83) * mm, "radius": 1.2 * mm});
            skCircle(sketch, "E6.18.20.0", {"center": v(117.48, 130.18) * mm, "radius": 1.2 * mm});
            skCircle(sketch, "E6.18.21.0", {"center": v(117.48, 136.53) * mm, "radius": 1.2 * mm});
            skCircle(sketch, "E6.18.22.0", {"center": v(117.48, 142.88) * mm, "radius": 1.2 * mm});
            skCircle(sketch, "E6.19.0.0", {"center": v(123.83, 3.17) * mm, "radius": 1.2 * mm});
            skCircle(sketch, "E6.19.1.0", {"center": v(123.83, 9.53) * mm, "radius": 1.2 * mm});
            skCircle(sketch, "E6.19.2.0", {"center": v(123.83, 15.88) * mm, "radius": 1.2 * mm});
            skCircle(sketch, "E6.19.3.0", {"center": v(123.83, 22.23) * mm, "radius": 1.2 * mm});
            skCircle(sketch, "E6.19.4.0", {"center": v(123.83, 28.58) * mm, "radius": 1.2 * mm});
            skCircle(sketch, "E6.19.5.0", {"center": v(123.83, 34.92) * mm, "radius": 1.2 * mm});
            skCircle(sketch, "E6.19.6.0", {"center": v(123.83, 41.27) * mm, "radius": 1.2 * mm});
            skCircle(sketch, "E6.19.7.0", {"center": v(123.83, 47.62) * mm, "radius": 1.2 * mm});
            skCircle(sketch, "E6.19.8.0", {"center": v(123.83, 53.98) * mm, "radius": 1.2 * mm});
            skCircle(sketch, "E6.19.9.0", {"center": v(123.83, 60.33) * mm, "radius": 1.2 * mm});
            skCircle(sketch, "E6.19.10.0", {"center": v(123.83, 66.67) * mm, "radius": 1.2 * mm});
            skCircle(sketch, "E6.19.11.0", {"center": v(123.83, 73.03) * mm, "radius": 1.2 * mm});
            skCircle(sketch, "E6.19.12.0", {"center": v(123.83, 79.38) * mm, "radius": 1.2 * mm});
            skCircle(sketch, "E6.19.13.0", {"center": v(123.83, 85.73) * mm, "radius": 1.2 * mm});
            skCircle(sketch, "E6.19.14.0", {"center": v(123.83, 92.08) * mm, "radius": 1.2 * mm});
            skCircle(sketch, "E6.19.15.0", {"center": v(123.83, 98.43) * mm, "radius": 1.2 * mm});
            skCircle(sketch, "E6.19.16.0", {"center": v(123.83, 104.78) * mm, "radius": 1.2 * mm});
            skCircle(sketch, "E6.19.17.0", {"center": v(123.83, 111.12) * mm, "radius": 1.2 * mm});
            skCircle(sketch, "E6.19.18.0", {"center": v(123.83, 117.48) * mm, "radius": 1.2 * mm});
            skCircle(sketch, "E6.19.19.0", {"center": v(123.83, 123.83) * mm, "radius": 1.2 * mm});
            skCircle(sketch, "E6.19.20.0", {"center": v(123.83, 130.18) * mm, "radius": 1.2 * mm});
            skCircle(sketch, "E6.19.21.0", {"center": v(123.83, 136.53) * mm, "radius": 1.2 * mm});
            skCircle(sketch, "E6.19.22.0", {"center": v(123.83, 142.88) * mm, "radius": 1.2 * mm});
            skCircle(sketch, "E6.20.0.0", {"center": v(130.18, 3.17) * mm, "radius": 1.2 * mm});
            skCircle(sketch, "E6.20.1.0", {"center": v(130.18, 9.53) * mm, "radius": 1.2 * mm});
            skCircle(sketch, "E6.20.2.0", {"center": v(130.18, 15.88) * mm, "radius": 1.2 * mm});
            skCircle(sketch, "E6.20.3.0", {"center": v(130.18, 22.23) * mm, "radius": 1.2 * mm});
            skCircle(sketch, "E6.20.4.0", {"center": v(130.18, 28.58) * mm, "radius": 1.2 * mm});
            skCircle(sketch, "E6.20.5.0", {"center": v(130.18, 34.92) * mm, "radius": 1.2 * mm});
            skCircle(sketch, "E6.20.6.0", {"center": v(130.18, 41.27) * mm, "radius": 1.2 * mm});
            skCircle(sketch, "E6.20.7.0", {"center": v(130.18, 47.62) * mm, "radius": 1.2 * mm});
            skCircle(sketch, "E6.20.8.0", {"center": v(130.18, 53.98) * mm, "radius": 1.2 * mm});
            skCircle(sketch, "E6.20.9.0", {"center": v(130.18, 60.33) * mm, "radius": 1.2 * mm});
            skCircle(sketch, "E6.20.10.0", {"center": v(130.18, 66.67) * mm, "radius": 1.2 * mm});
            skCircle(sketch, "E6.20.11.0", {"center": v(130.18, 73.03) * mm, "radius": 1.2 * mm});
            skCircle(sketch, "E6.20.12.0", {"center": v(130.18, 79.38) * mm, "radius": 1.2 * mm});
            skCircle(sketch, "E6.20.13.0", {"center": v(130.18, 85.73) * mm, "radius": 1.2 * mm});
            skCircle(sketch, "E6.20.14.0", {"center": v(130.18, 92.08) * mm, "radius": 1.2 * mm});
            skCircle(sketch, "E6.20.15.0", {"center": v(130.18, 98.43) * mm, "radius": 1.2 * mm});
            skCircle(sketch, "E6.20.16.0", {"center": v(130.18, 104.78) * mm, "radius": 1.2 * mm});
            skCircle(sketch, "E6.20.17.0", {"center": v(130.18, 111.12) * mm, "radius": 1.2 * mm});
            skCircle(sketch, "E6.20.18.0", {"center": v(130.18, 117.48) * mm, "radius": 1.2 * mm});
            skCircle(sketch, "E6.20.19.0", {"center": v(130.18, 123.83) * mm, "radius": 1.2 * mm});
            skCircle(sketch, "E6.20.20.0", {"center": v(130.18, 130.18) * mm, "radius": 1.2 * mm});
            skCircle(sketch, "E6.20.21.0", {"center": v(130.18, 136.53) * mm, "radius": 1.2 * mm});
            skCircle(sketch, "E6.20.22.0", {"center": v(130.18, 142.88) * mm, "radius": 1.2 * mm});
            skCircle(sketch, "E6.21.0.0", {"center": v(136.53, 3.17) * mm, "radius": 1.2 * mm});
            skCircle(sketch, "E6.21.1.0", {"center": v(136.53, 9.53) * mm, "radius": 1.2 * mm});
            skCircle(sketch, "E6.21.2.0", {"center": v(136.53, 15.88) * mm, "radius": 1.2 * mm});
            skCircle(sketch, "E6.21.3.0", {"center": v(136.53, 22.23) * mm, "radius": 1.2 * mm});
            skCircle(sketch, "E6.21.4.0", {"center": v(136.53, 28.58) * mm, "radius": 1.2 * mm});
            skCircle(sketch, "E6.21.5.0", {"center": v(136.53, 34.92) * mm, "radius": 1.2 * mm});
            skCircle(sketch, "E6.21.6.0", {"center": v(136.53, 41.27) * mm, "radius": 1.2 * mm});
            skCircle(sketch, "E6.21.7.0", {"center": v(136.53, 47.62) * mm, "radius": 1.2 * mm});
            skCircle(sketch, "E6.21.8.0", {"center": v(136.53, 53.98) * mm, "radius": 1.2 * mm});
            skCircle(sketch, "E6.21.9.0", {"center": v(136.53, 60.33) * mm, "radius": 1.2 * mm});
            skCircle(sketch, "E6.21.10.0", {"center": v(136.53, 66.67) * mm, "radius": 1.2 * mm});
            skCircle(sketch, "E6.21.11.0", {"center": v(136.53, 73.03) * mm, "radius": 1.2 * mm});
            skCircle(sketch, "E6.21.12.0", {"center": v(136.53, 79.38) * mm, "radius": 1.2 * mm});
            skCircle(sketch, "E6.21.13.0", {"center": v(136.53, 85.73) * mm, "radius": 1.2 * mm});
            skCircle(sketch, "E6.21.14.0", {"center": v(136.53, 92.08) * mm, "radius": 1.2 * mm});
            skCircle(sketch, "E6.21.15.0", {"center": v(136.53, 98.43) * mm, "radius": 1.2 * mm});
            skCircle(sketch, "E6.21.16.0", {"center": v(136.53, 104.78) * mm, "radius": 1.2 * mm});
            skCircle(sketch, "E6.21.17.0", {"center": v(136.53, 111.12) * mm, "radius": 1.2 * mm});
            skCircle(sketch, "E6.21.18.0", {"center": v(136.53, 117.48) * mm, "radius": 1.2 * mm});
            skCircle(sketch, "E6.21.19.0", {"center": v(136.53, 123.83) * mm, "radius": 1.2 * mm});
            skCircle(sketch, "E6.21.20.0", {"center": v(136.53, 130.18) * mm, "radius": 1.2 * mm});
            skCircle(sketch, "E6.21.21.0", {"center": v(136.53, 136.53) * mm, "radius": 1.2 * mm});
            skCircle(sketch, "E6.21.22.0", {"center": v(136.53, 142.88) * mm, "radius": 1.2 * mm});
            skCircle(sketch, "E6.22.0.0", {"center": v(142.88, 3.17) * mm, "radius": 1.2 * mm});
            skCircle(sketch, "E6.22.1.0", {"center": v(142.88, 9.53) * mm, "radius": 1.2 * mm});
            skCircle(sketch, "E6.22.2.0", {"center": v(142.88, 15.88) * mm, "radius": 1.2 * mm});
            skCircle(sketch, "E6.22.3.0", {"center": v(142.88, 22.23) * mm, "radius": 1.2 * mm});
            skCircle(sketch, "E6.22.4.0", {"center": v(142.88, 28.58) * mm, "radius": 1.2 * mm});
            skCircle(sketch, "E6.22.5.0", {"center": v(142.88, 34.92) * mm, "radius": 1.2 * mm});
            skCircle(sketch, "E6.22.6.0", {"center": v(142.88, 41.27) * mm, "radius": 1.2 * mm});
            skCircle(sketch, "E6.22.7.0", {"center": v(142.88, 47.62) * mm, "radius": 1.2 * mm});
            skCircle(sketch, "E6.22.8.0", {"center": v(142.88, 53.98) * mm, "radius": 1.2 * mm});
            skCircle(sketch, "E6.22.9.0", {"center": v(142.88, 60.33) * mm, "radius": 1.2 * mm});
            skCircle(sketch, "E6.22.10.0", {"center": v(142.88, 66.67) * mm, "radius": 1.2 * mm});
            skCircle(sketch, "E6.22.11.0", {"center": v(142.88, 73.03) * mm, "radius": 1.2 * mm});
            skCircle(sketch, "E6.22.12.0", {"center": v(142.88, 79.38) * mm, "radius": 1.2 * mm});
            skCircle(sketch, "E6.22.13.0", {"center": v(142.88, 85.73) * mm, "radius": 1.2 * mm});
            skCircle(sketch, "E6.22.14.0", {"center": v(142.88, 92.08) * mm, "radius": 1.2 * mm});
            skCircle(sketch, "E6.22.15.0", {"center": v(142.88, 98.43) * mm, "radius": 1.2 * mm});
            skCircle(sketch, "E6.22.16.0", {"center": v(142.88, 104.78) * mm, "radius": 1.2 * mm});
            skCircle(sketch, "E6.22.17.0", {"center": v(142.88, 111.12) * mm, "radius": 1.2 * mm});
            skCircle(sketch, "E6.22.18.0", {"center": v(142.88, 117.48) * mm, "radius": 1.2 * mm});
            skCircle(sketch, "E6.22.19.0", {"center": v(142.88, 123.83) * mm, "radius": 1.2 * mm});
            skCircle(sketch, "E6.22.20.0", {"center": v(142.88, 130.18) * mm, "radius": 1.2 * mm});
            skCircle(sketch, "E6.22.21.0", {"center": v(142.88, 136.53) * mm, "radius": 1.2 * mm});
            skCircle(sketch, "E6.22.22.0", {"center": v(142.88, 142.88) * mm, "radius": 1.2 * mm});
            skCircle(sketch, "E6.23.0.0", {"center": v(149.23, 3.17) * mm, "radius": 1.2 * mm});
            skCircle(sketch, "E6.23.1.0", {"center": v(149.23, 9.53) * mm, "radius": 1.2 * mm});
            skCircle(sketch, "E6.23.2.0", {"center": v(149.23, 15.88) * mm, "radius": 1.2 * mm});
            skCircle(sketch, "E6.23.3.0", {"center": v(149.23, 22.23) * mm, "radius": 1.2 * mm});
            skCircle(sketch, "E6.23.4.0", {"center": v(149.23, 28.58) * mm, "radius": 1.2 * mm});
            skCircle(sketch, "E6.23.5.0", {"center": v(149.23, 34.92) * mm, "radius": 1.2 * mm});
            skCircle(sketch, "E6.23.6.0", {"center": v(149.23, 41.27) * mm, "radius": 1.2 * mm});
            skCircle(sketch, "E6.23.7.0", {"center": v(149.23, 47.62) * mm, "radius": 1.2 * mm});
            skCircle(sketch, "E6.23.8.0", {"center": v(149.23, 53.98) * mm, "radius": 1.2 * mm});
            skCircle(sketch, "E6.23.9.0", {"center": v(149.23, 60.33) * mm, "radius": 1.2 * mm});
            skCircle(sketch, "E6.23.10.0", {"center": v(149.23, 66.67) * mm, "radius": 1.2 * mm});
            skCircle(sketch, "E6.23.11.0", {"center": v(149.23, 73.03) * mm, "radius": 1.2 * mm});
            skCircle(sketch, "E6.23.12.0", {"center": v(149.23, 79.38) * mm, "radius": 1.2 * mm});
            skCircle(sketch, "E6.23.13.0", {"center": v(149.23, 85.73) * mm, "radius": 1.2 * mm});
            skCircle(sketch, "E6.23.14.0", {"center": v(149.23, 92.08) * mm, "radius": 1.2 * mm});
            skCircle(sketch, "E6.23.15.0", {"center": v(149.23, 98.43) * mm, "radius": 1.2 * mm});
            skCircle(sketch, "E6.23.16.0", {"center": v(149.23, 104.78) * mm, "radius": 1.2 * mm});
            skCircle(sketch, "E6.23.17.0", {"center": v(149.23, 111.12) * mm, "radius": 1.2 * mm});
            skCircle(sketch, "E6.23.18.0", {"center": v(149.23, 117.48) * mm, "radius": 1.2 * mm});
            skCircle(sketch, "E6.23.19.0", {"center": v(149.23, 123.83) * mm, "radius": 1.2 * mm});
            skCircle(sketch, "E6.23.20.0", {"center": v(149.23, 130.18) * mm, "radius": 1.2 * mm});
            skCircle(sketch, "E6.23.21.0", {"center": v(149.23, 136.53) * mm, "radius": 1.2 * mm});
            skCircle(sketch, "E6.23.22.0", {"center": v(149.23, 142.88) * mm, "radius": 1.2 * mm});
            skCircle(sketch, "E6.24.0.0", {"center": v(155.58, 3.17) * mm, "radius": 1.2 * mm});
            skCircle(sketch, "E6.24.1.0", {"center": v(155.58, 9.53) * mm, "radius": 1.2 * mm});
            skCircle(sketch, "E6.24.2.0", {"center": v(155.58, 15.88) * mm, "radius": 1.2 * mm});
            skCircle(sketch, "E6.24.3.0", {"center": v(155.58, 22.23) * mm, "radius": 1.2 * mm});
            skCircle(sketch, "E6.24.4.0", {"center": v(155.58, 28.58) * mm, "radius": 1.2 * mm});
            skCircle(sketch, "E6.24.5.0", {"center": v(155.58, 34.92) * mm, "radius": 1.2 * mm});
            skCircle(sketch, "E6.24.6.0", {"center": v(155.58, 41.27) * mm, "radius": 1.2 * mm});
            skCircle(sketch, "E6.24.7.0", {"center": v(155.58, 47.62) * mm, "radius": 1.2 * mm});
            skCircle(sketch, "E6.24.8.0", {"center": v(155.58, 53.98) * mm, "radius": 1.2 * mm});
            skCircle(sketch, "E6.24.9.0", {"center": v(155.58, 60.33) * mm, "radius": 1.2 * mm});
            skCircle(sketch, "E6.24.10.0", {"center": v(155.58, 66.67) * mm, "radius": 1.2 * mm});
            skCircle(sketch, "E6.24.11.0", {"center": v(155.58, 73.03) * mm, "radius": 1.2 * mm});
            skCircle(sketch, "E6.24.12.0", {"center": v(155.58, 79.38) * mm, "radius": 1.2 * mm});
            skCircle(sketch, "E6.24.13.0", {"center": v(155.58, 85.73) * mm, "radius": 1.2 * mm});
            skCircle(sketch, "E6.24.14.0", {"center": v(155.58, 92.08) * mm, "radius": 1.2 * mm});
            skCircle(sketch, "E6.24.15.0", {"center": v(155.58, 98.43) * mm, "radius": 1.2 * mm});
            skCircle(sketch, "E6.24.16.0", {"center": v(155.58, 104.78) * mm, "radius": 1.2 * mm});
            skCircle(sketch, "E6.24.17.0", {"center": v(155.58, 111.12) * mm, "radius": 1.2 * mm});
            skCircle(sketch, "E6.24.18.0", {"center": v(155.58, 117.48) * mm, "radius": 1.2 * mm});
            skCircle(sketch, "E6.24.19.0", {"center": v(155.58, 123.83) * mm, "radius": 1.2 * mm});
            skCircle(sketch, "E6.24.20.0", {"center": v(155.58, 130.18) * mm, "radius": 1.2 * mm});
            skCircle(sketch, "E6.24.21.0", {"center": v(155.58, 136.53) * mm, "radius": 1.2 * mm});
            skCircle(sketch, "E6.24.22.0", {"center": v(155.58, 142.88) * mm, "radius": 1.2 * mm});
            skCircle(sketch, "E6.25.0.0", {"center": v(161.93, 3.17) * mm, "radius": 1.2 * mm});
            skCircle(sketch, "E6.25.1.0", {"center": v(161.93, 9.53) * mm, "radius": 1.2 * mm});
            skCircle(sketch, "E6.25.2.0", {"center": v(161.93, 15.88) * mm, "radius": 1.2 * mm});
            skCircle(sketch, "E6.25.3.0", {"center": v(161.93, 22.23) * mm, "radius": 1.2 * mm});
            skCircle(sketch, "E6.25.4.0", {"center": v(161.93, 28.58) * mm, "radius": 1.2 * mm});
            skCircle(sketch, "E6.25.5.0", {"center": v(161.93, 34.92) * mm, "radius": 1.2 * mm});
            skCircle(sketch, "E6.25.6.0", {"center": v(161.93, 41.27) * mm, "radius": 1.2 * mm});
            skCircle(sketch, "E6.25.7.0", {"center": v(161.93, 47.62) * mm, "radius": 1.2 * mm});
            skCircle(sketch, "E6.25.8.0", {"center": v(161.93, 53.98) * mm, "radius": 1.2 * mm});
            skCircle(sketch, "E6.25.9.0", {"center": v(161.93, 60.33) * mm, "radius": 1.2 * mm});
            skCircle(sketch, "E6.25.10.0", {"center": v(161.93, 66.67) * mm, "radius": 1.2 * mm});
            skCircle(sketch, "E6.25.11.0", {"center": v(161.93, 73.03) * mm, "radius": 1.2 * mm});
            skCircle(sketch, "E6.25.12.0", {"center": v(161.93, 79.38) * mm, "radius": 1.2 * mm});
            skCircle(sketch, "E6.25.13.0", {"center": v(161.93, 85.73) * mm, "radius": 1.2 * mm});
            skCircle(sketch, "E6.25.14.0", {"center": v(161.93, 92.08) * mm, "radius": 1.2 * mm});
            skCircle(sketch, "E6.25.15.0", {"center": v(161.93, 98.43) * mm, "radius": 1.2 * mm});
            skCircle(sketch, "E6.25.16.0", {"center": v(161.93, 104.78) * mm, "radius": 1.2 * mm});
            skCircle(sketch, "E6.25.17.0", {"center": v(161.93, 111.12) * mm, "radius": 1.2 * mm});
            skCircle(sketch, "E6.25.18.0", {"center": v(161.93, 117.48) * mm, "radius": 1.2 * mm});
            skCircle(sketch, "E6.25.19.0", {"center": v(161.93, 123.83) * mm, "radius": 1.2 * mm});
            skCircle(sketch, "E6.25.20.0", {"center": v(161.93, 130.18) * mm, "radius": 1.2 * mm});
            skCircle(sketch, "E6.25.21.0", {"center": v(161.93, 136.53) * mm, "radius": 1.2 * mm});
            skCircle(sketch, "E6.25.22.0", {"center": v(161.93, 142.88) * mm, "radius": 1.2 * mm});
            skCircle(sketch, "E6.26.0.0", {"center": v(168.28, 3.17) * mm, "radius": 1.2 * mm});
            skCircle(sketch, "E6.26.1.0", {"center": v(168.28, 9.53) * mm, "radius": 1.2 * mm});
            skCircle(sketch, "E6.26.2.0", {"center": v(168.28, 15.88) * mm, "radius": 1.2 * mm});
            skCircle(sketch, "E6.26.3.0", {"center": v(168.28, 22.23) * mm, "radius": 1.2 * mm});
            skCircle(sketch, "E6.26.4.0", {"center": v(168.28, 28.58) * mm, "radius": 1.2 * mm});
            skCircle(sketch, "E6.26.5.0", {"center": v(168.28, 34.92) * mm, "radius": 1.2 * mm});
            skCircle(sketch, "E6.26.6.0", {"center": v(168.28, 41.27) * mm, "radius": 1.2 * mm});
            skCircle(sketch, "E6.26.7.0", {"center": v(168.28, 47.62) * mm, "radius": 1.2 * mm});
            skCircle(sketch, "E6.26.8.0", {"center": v(168.28, 53.98) * mm, "radius": 1.2 * mm});
            skCircle(sketch, "E6.26.9.0", {"center": v(168.28, 60.33) * mm, "radius": 1.2 * mm});
            skCircle(sketch, "E6.26.10.0", {"center": v(168.28, 66.67) * mm, "radius": 1.2 * mm});
            skCircle(sketch, "E6.26.11.0", {"center": v(168.28, 73.03) * mm, "radius": 1.2 * mm});
            skCircle(sketch, "E6.26.12.0", {"center": v(168.28, 79.38) * mm, "radius": 1.2 * mm});
            skCircle(sketch, "E6.26.13.0", {"center": v(168.28, 85.73) * mm, "radius": 1.2 * mm});
            skCircle(sketch, "E6.26.14.0", {"center": v(168.28, 92.08) * mm, "radius": 1.2 * mm});
            skCircle(sketch, "E6.26.15.0", {"center": v(168.28, 98.43) * mm, "radius": 1.2 * mm});
            skCircle(sketch, "E6.26.16.0", {"center": v(168.28, 104.78) * mm, "radius": 1.2 * mm});
            skCircle(sketch, "E6.26.17.0", {"center": v(168.28, 111.12) * mm, "radius": 1.2 * mm});
            skCircle(sketch, "E6.26.18.0", {"center": v(168.28, 117.48) * mm, "radius": 1.2 * mm});
            skCircle(sketch, "E6.26.19.0", {"center": v(168.28, 123.83) * mm, "radius": 1.2 * mm});
            skCircle(sketch, "E6.26.20.0", {"center": v(168.28, 130.18) * mm, "radius": 1.2 * mm});
            skCircle(sketch, "E6.26.21.0", {"center": v(168.28, 136.53) * mm, "radius": 1.2 * mm});
            skCircle(sketch, "E6.26.22.0", {"center": v(168.28, 142.88) * mm, "radius": 1.2 * mm});
            skCircle(sketch, "E6.27.0.0", {"center": v(174.63, 3.17) * mm, "radius": 1.2 * mm});
            skCircle(sketch, "E6.27.1.0", {"center": v(174.63, 9.53) * mm, "radius": 1.2 * mm});
            skCircle(sketch, "E6.27.2.0", {"center": v(174.63, 15.88) * mm, "radius": 1.2 * mm});
            skCircle(sketch, "E6.27.3.0", {"center": v(174.63, 22.23) * mm, "radius": 1.2 * mm});
            skCircle(sketch, "E6.27.4.0", {"center": v(174.63, 28.58) * mm, "radius": 1.2 * mm});
            skCircle(sketch, "E6.27.5.0", {"center": v(174.63, 34.92) * mm, "radius": 1.2 * mm});
            skCircle(sketch, "E6.27.6.0", {"center": v(174.63, 41.27) * mm, "radius": 1.2 * mm});
            skCircle(sketch, "E6.27.7.0", {"center": v(174.63, 47.62) * mm, "radius": 1.2 * mm});
            skCircle(sketch, "E6.27.8.0", {"center": v(174.63, 53.98) * mm, "radius": 1.2 * mm});
            skCircle(sketch, "E6.27.9.0", {"center": v(174.63, 60.33) * mm, "radius": 1.2 * mm});
            skCircle(sketch, "E6.27.10.0", {"center": v(174.63, 66.67) * mm, "radius": 1.2 * mm});
            skCircle(sketch, "E6.27.11.0", {"center": v(174.63, 73.03) * mm, "radius": 1.2 * mm});
            skCircle(sketch, "E6.27.12.0", {"center": v(174.63, 79.38) * mm, "radius": 1.2 * mm});
            skCircle(sketch, "E6.27.13.0", {"center": v(174.63, 85.73) * mm, "radius": 1.2 * mm});
            skCircle(sketch, "E6.27.14.0", {"center": v(174.63, 92.08) * mm, "radius": 1.2 * mm});
            skCircle(sketch, "E6.27.15.0", {"center": v(174.63, 98.43) * mm, "radius": 1.2 * mm});
            skCircle(sketch, "E6.27.16.0", {"center": v(174.63, 104.78) * mm, "radius": 1.2 * mm});
            skCircle(sketch, "E6.27.17.0", {"center": v(174.63, 111.12) * mm, "radius": 1.2 * mm});
            skCircle(sketch, "E6.27.18.0", {"center": v(174.63, 117.48) * mm, "radius": 1.2 * mm});
            skCircle(sketch, "E6.27.19.0", {"center": v(174.63, 123.83) * mm, "radius": 1.2 * mm});
            skCircle(sketch, "E6.27.20.0", {"center": v(174.63, 130.18) * mm, "radius": 1.2 * mm});
            skCircle(sketch, "E6.27.21.0", {"center": v(174.63, 136.53) * mm, "radius": 1.2 * mm});
            skCircle(sketch, "E6.27.22.0", {"center": v(174.63, 142.88) * mm, "radius": 1.2 * mm});
            skCircle(sketch, "E6.28.0.0", {"center": v(180.98, 3.17) * mm, "radius": 1.2 * mm});
            skCircle(sketch, "E6.28.1.0", {"center": v(180.98, 9.53) * mm, "radius": 1.2 * mm});
            skCircle(sketch, "E6.28.2.0", {"center": v(180.98, 15.88) * mm, "radius": 1.2 * mm});
            skCircle(sketch, "E6.28.3.0", {"center": v(180.98, 22.23) * mm, "radius": 1.2 * mm});
            skCircle(sketch, "E6.28.4.0", {"center": v(180.98, 28.58) * mm, "radius": 1.2 * mm});
            skCircle(sketch, "E6.28.5.0", {"center": v(180.98, 34.92) * mm, "radius": 1.2 * mm});
            skCircle(sketch, "E6.28.6.0", {"center": v(180.98, 41.27) * mm, "radius": 1.2 * mm});
            skCircle(sketch, "E6.28.7.0", {"center": v(180.98, 47.62) * mm, "radius": 1.2 * mm});
            skCircle(sketch, "E6.28.8.0", {"center": v(180.98, 53.98) * mm, "radius": 1.2 * mm});
            skCircle(sketch, "E6.28.9.0", {"center": v(180.98, 60.33) * mm, "radius": 1.2 * mm});
            skCircle(sketch, "E6.28.10.0", {"center": v(180.98, 66.67) * mm, "radius": 1.2 * mm});
            skCircle(sketch, "E6.28.11.0", {"center": v(180.98, 73.03) * mm, "radius": 1.2 * mm});
            skCircle(sketch, "E6.28.12.0", {"center": v(180.98, 79.38) * mm, "radius": 1.2 * mm});
            skCircle(sketch, "E6.28.13.0", {"center": v(180.98, 85.73) * mm, "radius": 1.2 * mm});
            skCircle(sketch, "E6.28.14.0", {"center": v(180.98, 92.08) * mm, "radius": 1.2 * mm});
            skCircle(sketch, "E6.28.15.0", {"center": v(180.98, 98.43) * mm, "radius": 1.2 * mm});
            skCircle(sketch, "E6.28.16.0", {"center": v(180.98, 104.78) * mm, "radius": 1.2 * mm});
            skCircle(sketch, "E6.28.17.0", {"center": v(180.98, 111.12) * mm, "radius": 1.2 * mm});
            skCircle(sketch, "E6.28.18.0", {"center": v(180.98, 117.48) * mm, "radius": 1.2 * mm});
            skCircle(sketch, "E6.28.19.0", {"center": v(180.98, 123.83) * mm, "radius": 1.2 * mm});
            skCircle(sketch, "E6.28.20.0", {"center": v(180.98, 130.18) * mm, "radius": 1.2 * mm});
            skCircle(sketch, "E6.28.21.0", {"center": v(180.98, 136.53) * mm, "radius": 1.2 * mm});
            skCircle(sketch, "E6.28.22.0", {"center": v(180.98, 142.88) * mm, "radius": 1.2 * mm});
            skCircle(sketch, "E6.29.0.0", {"center": v(187.33, 3.17) * mm, "radius": 1.2 * mm});
            skCircle(sketch, "E6.29.1.0", {"center": v(187.33, 9.53) * mm, "radius": 1.2 * mm});
            skCircle(sketch, "E6.29.2.0", {"center": v(187.33, 15.88) * mm, "radius": 1.2 * mm});
            skCircle(sketch, "E6.29.3.0", {"center": v(187.33, 22.23) * mm, "radius": 1.2 * mm});
            skCircle(sketch, "E6.29.4.0", {"center": v(187.33, 28.58) * mm, "radius": 1.2 * mm});
            skCircle(sketch, "E6.29.5.0", {"center": v(187.33, 34.92) * mm, "radius": 1.2 * mm});
            skCircle(sketch, "E6.29.6.0", {"center": v(187.33, 41.27) * mm, "radius": 1.2 * mm});
            skCircle(sketch, "E6.29.7.0", {"center": v(187.33, 47.62) * mm, "radius": 1.2 * mm});
            skCircle(sketch, "E6.29.8.0", {"center": v(187.33, 53.98) * mm, "radius": 1.2 * mm});
            skCircle(sketch, "E6.29.9.0", {"center": v(187.33, 60.33) * mm, "radius": 1.2 * mm});
            skCircle(sketch, "E6.29.10.0", {"center": v(187.33, 66.67) * mm, "radius": 1.2 * mm});
            skCircle(sketch, "E6.29.11.0", {"center": v(187.33, 73.03) * mm, "radius": 1.2 * mm});
            skCircle(sketch, "E6.29.12.0", {"center": v(187.33, 79.38) * mm, "radius": 1.2 * mm});
            skCircle(sketch, "E6.29.13.0", {"center": v(187.33, 85.73) * mm, "radius": 1.2 * mm});
            skCircle(sketch, "E6.29.14.0", {"center": v(187.33, 92.08) * mm, "radius": 1.2 * mm});
            skCircle(sketch, "E6.29.15.0", {"center": v(187.33, 98.43) * mm, "radius": 1.2 * mm});
            skCircle(sketch, "E6.29.16.0", {"center": v(187.33, 104.78) * mm, "radius": 1.2 * mm});
            skCircle(sketch, "E6.29.17.0", {"center": v(187.33, 111.12) * mm, "radius": 1.2 * mm});
            skCircle(sketch, "E6.29.18.0", {"center": v(187.33, 117.48) * mm, "radius": 1.2 * mm});
            skCircle(sketch, "E6.29.19.0", {"center": v(187.33, 123.83) * mm, "radius": 1.2 * mm});
            skCircle(sketch, "E6.29.20.0", {"center": v(187.33, 130.18) * mm, "radius": 1.2 * mm});
            skCircle(sketch, "E6.29.21.0", {"center": v(187.33, 136.53) * mm, "radius": 1.2 * mm});
            skCircle(sketch, "E6.29.22.0", {"center": v(187.33, 142.88) * mm, "radius": 1.2 * mm});
            skCircle(sketch, "E6.30.0.0", {"center": v(193.68, 3.17) * mm, "radius": 1.2 * mm});
            skCircle(sketch, "E6.30.1.0", {"center": v(193.68, 9.53) * mm, "radius": 1.2 * mm});
            skCircle(sketch, "E6.30.2.0", {"center": v(193.68, 15.88) * mm, "radius": 1.2 * mm});
            skCircle(sketch, "E6.30.3.0", {"center": v(193.68, 22.23) * mm, "radius": 1.2 * mm});
            skCircle(sketch, "E6.30.4.0", {"center": v(193.68, 28.58) * mm, "radius": 1.2 * mm});
            skCircle(sketch, "E6.30.5.0", {"center": v(193.68, 34.92) * mm, "radius": 1.2 * mm});
            skCircle(sketch, "E6.30.6.0", {"center": v(193.68, 41.27) * mm, "radius": 1.2 * mm});
            skCircle(sketch, "E6.30.7.0", {"center": v(193.68, 47.62) * mm, "radius": 1.2 * mm});
            skCircle(sketch, "E6.30.8.0", {"center": v(193.68, 53.98) * mm, "radius": 1.2 * mm});
            skCircle(sketch, "E6.30.9.0", {"center": v(193.68, 60.33) * mm, "radius": 1.2 * mm});
            skCircle(sketch, "E6.30.10.0", {"center": v(193.68, 66.67) * mm, "radius": 1.2 * mm});
            skCircle(sketch, "E6.30.11.0", {"center": v(193.68, 73.03) * mm, "radius": 1.2 * mm});
            skCircle(sketch, "E6.30.12.0", {"center": v(193.68, 79.38) * mm, "radius": 1.2 * mm});
            skCircle(sketch, "E6.30.13.0", {"center": v(193.68, 85.73) * mm, "radius": 1.2 * mm});
            skCircle(sketch, "E6.30.14.0", {"center": v(193.68, 92.08) * mm, "radius": 1.2 * mm});
            skCircle(sketch, "E6.30.15.0", {"center": v(193.68, 98.43) * mm, "radius": 1.2 * mm});
            skCircle(sketch, "E6.30.16.0", {"center": v(193.68, 104.78) * mm, "radius": 1.2 * mm});
            skCircle(sketch, "E6.30.17.0", {"center": v(193.68, 111.12) * mm, "radius": 1.2 * mm});
            skCircle(sketch, "E6.30.18.0", {"center": v(193.68, 117.48) * mm, "radius": 1.2 * mm});
            skCircle(sketch, "E6.30.19.0", {"center": v(193.68, 123.83) * mm, "radius": 1.2 * mm});
            skCircle(sketch, "E6.30.20.0", {"center": v(193.68, 130.18) * mm, "radius": 1.2 * mm});
            skCircle(sketch, "E6.30.21.0", {"center": v(193.68, 136.53) * mm, "radius": 1.2 * mm});
            skCircle(sketch, "E6.30.22.0", {"center": v(193.68, 142.88) * mm, "radius": 1.2 * mm});
            skCircle(sketch, "E6.31.0.0", {"center": v(200.03, 3.17) * mm, "radius": 1.2 * mm});
            skCircle(sketch, "E6.31.1.0", {"center": v(200.03, 9.53) * mm, "radius": 1.2 * mm});
            skCircle(sketch, "E6.31.2.0", {"center": v(200.03, 15.88) * mm, "radius": 1.2 * mm});
            skCircle(sketch, "E6.31.3.0", {"center": v(200.03, 22.23) * mm, "radius": 1.2 * mm});
            skCircle(sketch, "E6.31.4.0", {"center": v(200.03, 28.58) * mm, "radius": 1.2 * mm});
            skCircle(sketch, "E6.31.5.0", {"center": v(200.03, 34.92) * mm, "radius": 1.2 * mm});
            skCircle(sketch, "E6.31.6.0", {"center": v(200.03, 41.27) * mm, "radius": 1.2 * mm});
            skCircle(sketch, "E6.31.7.0", {"center": v(200.03, 47.62) * mm, "radius": 1.2 * mm});
            skCircle(sketch, "E6.31.8.0", {"center": v(200.03, 53.98) * mm, "radius": 1.2 * mm});
            skCircle(sketch, "E6.31.9.0", {"center": v(200.03, 60.33) * mm, "radius": 1.2 * mm});
            skCircle(sketch, "E6.31.10.0", {"center": v(200.03, 66.67) * mm, "radius": 1.2 * mm});
            skCircle(sketch, "E6.31.11.0", {"center": v(200.03, 73.03) * mm, "radius": 1.2 * mm});
            skCircle(sketch, "E6.31.12.0", {"center": v(200.03, 79.38) * mm, "radius": 1.2 * mm});
            skCircle(sketch, "E6.31.13.0", {"center": v(200.03, 85.73) * mm, "radius": 1.2 * mm});
            skCircle(sketch, "E6.31.14.0", {"center": v(200.03, 92.08) * mm, "radius": 1.2 * mm});
            skCircle(sketch, "E6.31.15.0", {"center": v(200.03, 98.43) * mm, "radius": 1.2 * mm});
            skCircle(sketch, "E6.31.16.0", {"center": v(200.03, 104.78) * mm, "radius": 1.2 * mm});
            skCircle(sketch, "E6.31.17.0", {"center": v(200.03, 111.12) * mm, "radius": 1.2 * mm});
            skCircle(sketch, "E6.31.18.0", {"center": v(200.03, 117.48) * mm, "radius": 1.2 * mm});
            skCircle(sketch, "E6.31.19.0", {"center": v(200.03, 123.83) * mm, "radius": 1.2 * mm});
            skCircle(sketch, "E6.31.20.0", {"center": v(200.03, 130.18) * mm, "radius": 1.2 * mm});
            skCircle(sketch, "E6.31.21.0", {"center": v(200.03, 136.53) * mm, "radius": 1.2 * mm});
            skCircle(sketch, "E6.31.22.0", {"center": v(200.03, 142.88) * mm, "radius": 1.2 * mm});
            skLineSegment(sketch, "E6.direction1", {"start": v(3.17, 3.17) * mm, "end": v(9.53, 3.17) * mm, "construction": true});
            skLineSegment(sketch, "E6.direction2", {"start": v(3.17, 3.17) * mm, "end": v(3.17, 9.53) * mm, "construction": true});
            skSolve(sketch);
        }
        {
            var Q0;
            Q0 = qSketchRegion(id + "F2", true);
            extrude(context, id + "F3", {"entities" : qUnion([Q0]), "operationType" : NewBodyOperationType.REMOVE, "endBound" : BoundingType.THROUGH_ALL, "oppositeDirection" : true, "depth" : 25.4 * mm});
        }
    });
